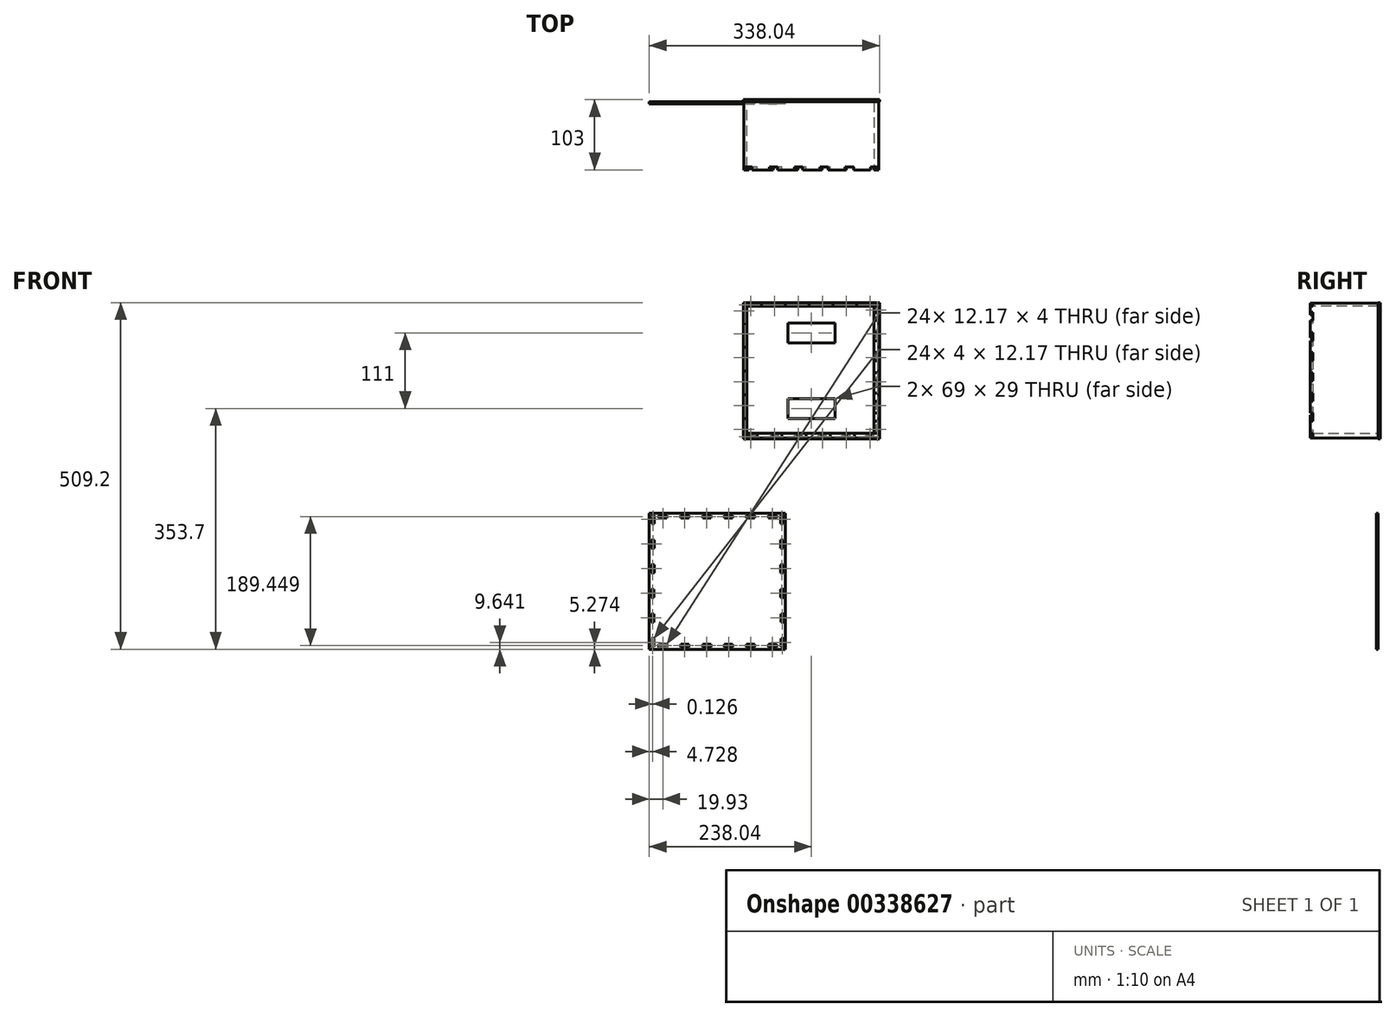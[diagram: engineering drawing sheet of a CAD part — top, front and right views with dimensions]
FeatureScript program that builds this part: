
annotation { "Feature Type Name" : "Feature", "Feature Type Description" : "" }
export const myFeature = defineFeature(function(context is Context, id is Id, definition is map)
    precondition{}
    {
        {
            var Q0;
            Q0=qCreatedBy(makeId("Front.planeOp"),FACE);
            var sketch = newSketch(context, id + "F0", { "sketchPlane" : qUnion([Q0])});
            skLineSegment(sketch, "E0.bottom", {"start": v(-100, 100) * mm, "end": v(100, 100) * mm});
            skLineSegment(sketch, "E0.top", {"start": v(-100, -100) * mm, "end": v(100, -100) * mm});
            skLineSegment(sketch, "E0.left", {"start": v(-100, 100) * mm, "end": v(-100, -100) * mm});
            skLineSegment(sketch, "E0.right", {"start": v(100, 100) * mm, "end": v(100, -100) * mm});
            skPoint(sketch, "E0.middle", {"position": v(0, 0) * mm});
            skLineSegment(sketch, "E1.0", {"start": v(-95, 95) * mm, "end": v(95, 95) * mm, "construction": true});
            skLineSegment(sketch, "E1.1", {"start": v(-95, 95) * mm, "end": v(-95, -95) * mm, "construction": true});
            skLineSegment(sketch, "E1.2", {"start": v(-95, -95) * mm, "end": v(95, -95) * mm, "construction": true});
            skLineSegment(sketch, "E1.3", {"start": v(95, 95) * mm, "end": v(95, -95) * mm, "construction": true});
            skSolve(sketch);
        }
        {
            var Q0;
            Q0 = qSketchRegion(id + "F0", true);
            extrude(context, id + "F1", {"entities" : qUnion([Q0]), "depth" : 3 * mm, "offsetDistance" : 25 * mm});
        }
        {
            var Q0;
            Q0=makeQuery(id+"F1.opExtrude","CAP_FACE",FACE,{"disambiguationData":[OSD([sQuery(id+"F0.wireOp",EDGE,"E0.bottom"),sQuery(id+"F0.wireOp",EDGE,"E0.top"),sQuery(id+"F0.wireOp",EDGE,"E0.left"),sQuery(id+"F0.wireOp",EDGE,"E0.right")])],"isStart":false});
            var sketch = newSketch(context, id + "F2", { "sketchPlane" : qUnion([Q0])});
            skLineSegment(sketch, "E2.0", {"start": v(-95, 95) * mm, "end": v(95, 95) * mm, "construction": true});
            skLineSegment(sketch, "E3.0", {"start": v(-95, 95) * mm, "end": v(-95, -95) * mm, "construction": true});
            skLineSegment(sketch, "E4.0", {"start": v(95, 95) * mm, "end": v(95, -95) * mm, "construction": true});
            skLineSegment(sketch, "E5.0", {"start": v(-95, -95) * mm, "end": v(95, -95) * mm, "construction": true});
            skLineSegment(sketch, "E6.bottom", {"start": v(-95, 99) * mm, "end": v(-82.83, 99) * mm});
            skLineSegment(sketch, "E6.top", {"start": v(-95, 95) * mm, "end": v(-82.83, 95) * mm});
            skLineSegment(sketch, "E6.left", {"start": v(-95, 99) * mm, "end": v(-95, 95) * mm});
            skLineSegment(sketch, "E6.right", {"start": v(-82.83, 99) * mm, "end": v(-82.83, 95) * mm});
            skLineSegment(sketch, "E7.1.0.0", {"start": v(-60, 99) * mm, "end": v(-47.83, 99) * mm});
            skLineSegment(sketch, "E7.1.0.1", {"start": v(-60, 99) * mm, "end": v(-60, 95) * mm});
            skLineSegment(sketch, "E7.1.0.2", {"start": v(-47.83, 99) * mm, "end": v(-47.83, 95) * mm});
            skLineSegment(sketch, "E7.1.0.3", {"start": v(-60, 95) * mm, "end": v(-47.83, 95) * mm});
            skLineSegment(sketch, "E7.2.0.0", {"start": v(-25, 99) * mm, "end": v(-12.83, 99) * mm});
            skLineSegment(sketch, "E7.2.0.1", {"start": v(-25, 99) * mm, "end": v(-25, 95) * mm});
            skLineSegment(sketch, "E7.2.0.2", {"start": v(-12.83, 99) * mm, "end": v(-12.83, 95) * mm});
            skLineSegment(sketch, "E7.2.0.3", {"start": v(-25, 95) * mm, "end": v(-12.83, 95) * mm});
            skLineSegment(sketch, "E7.3.0.0", {"start": v(10, 99) * mm, "end": v(22.17, 99) * mm});
            skLineSegment(sketch, "E7.3.0.1", {"start": v(10, 99) * mm, "end": v(10, 95) * mm});
            skLineSegment(sketch, "E7.3.0.2", {"start": v(22.17, 99) * mm, "end": v(22.17, 95) * mm});
            skLineSegment(sketch, "E7.3.0.3", {"start": v(10, 95) * mm, "end": v(22.17, 95) * mm});
            skLineSegment(sketch, "E7.4.0.0", {"start": v(45, 99) * mm, "end": v(57.17, 99) * mm});
            skLineSegment(sketch, "E7.4.0.1", {"start": v(45, 99) * mm, "end": v(45, 95) * mm});
            skLineSegment(sketch, "E7.4.0.2", {"start": v(57.17, 99) * mm, "end": v(57.17, 95) * mm});
            skLineSegment(sketch, "E7.4.0.3", {"start": v(45, 95) * mm, "end": v(57.17, 95) * mm});
            skLineSegment(sketch, "E7.5.0.0", {"start": v(80, 99) * mm, "end": v(92.17, 99) * mm});
            skLineSegment(sketch, "E7.5.0.1", {"start": v(80, 99) * mm, "end": v(80, 95) * mm});
            skLineSegment(sketch, "E7.5.0.2", {"start": v(92.17, 99) * mm, "end": v(92.17, 95) * mm});
            skLineSegment(sketch, "E7.5.0.3", {"start": v(80, 95) * mm, "end": v(92.17, 95) * mm});
            skLineSegment(sketch, "E7.direction1", {"start": v(-95, 99) * mm, "end": v(-60, 99) * mm, "construction": true});
            skLineSegment(sketch, "E8", {"start": v(-95, 0) * mm, "end": v(95, 0) * mm});
            skLineSegment(sketch, "E9.MirrorCS", {"start": v(-95, -99) * mm, "end": v(-95, -95) * mm});
            skLineSegment(sketch, "E10.MirrorCS", {"start": v(-82.83, -99) * mm, "end": v(-82.83, -95) * mm});
            skLineSegment(sketch, "E11.MirrorCS", {"start": v(-95, -95) * mm, "end": v(-82.83, -95) * mm});
            skLineSegment(sketch, "E12.MirrorCS", {"start": v(-95, -99) * mm, "end": v(-82.83, -99) * mm});
            skLineSegment(sketch, "E13.MirrorCS", {"start": v(-60, -99) * mm, "end": v(-47.83, -99) * mm});
            skLineSegment(sketch, "E14.MirrorCS", {"start": v(-47.83, -99) * mm, "end": v(-47.83, -95) * mm});
            skLineSegment(sketch, "E15.MirrorCS", {"start": v(-60, -99) * mm, "end": v(-60, -95) * mm});
            skLineSegment(sketch, "E16.MirrorCS", {"start": v(-60, -95) * mm, "end": v(-47.83, -95) * mm});
            skLineSegment(sketch, "E17.MirrorCS", {"start": v(-25, -99) * mm, "end": v(-12.83, -99) * mm});
            skLineSegment(sketch, "E18.MirrorCS", {"start": v(-25, -99) * mm, "end": v(-25, -95) * mm});
            skLineSegment(sketch, "E19.MirrorCS", {"start": v(-12.83, -99) * mm, "end": v(-12.83, -95) * mm});
            skLineSegment(sketch, "E20.MirrorCS", {"start": v(-25, -95) * mm, "end": v(-12.83, -95) * mm});
            skLineSegment(sketch, "E21.MirrorCS", {"start": v(10, -99) * mm, "end": v(22.17, -99) * mm});
            skLineSegment(sketch, "E22.MirrorCS", {"start": v(22.17, -99) * mm, "end": v(22.17, -95) * mm});
            skLineSegment(sketch, "E23.MirrorCS", {"start": v(10, -99) * mm, "end": v(10, -95) * mm});
            skLineSegment(sketch, "E24.MirrorCS", {"start": v(10, -95) * mm, "end": v(22.17, -95) * mm});
            skLineSegment(sketch, "E25.MirrorCS", {"start": v(45, -99) * mm, "end": v(57.17, -99) * mm});
            skLineSegment(sketch, "E26.MirrorCS", {"start": v(45, -99) * mm, "end": v(45, -95) * mm});
            skLineSegment(sketch, "E27.MirrorCS", {"start": v(57.17, -99) * mm, "end": v(57.17, -95) * mm});
            skLineSegment(sketch, "E28.MirrorCS", {"start": v(45, -95) * mm, "end": v(57.17, -95) * mm});
            skLineSegment(sketch, "E29.MirrorCS", {"start": v(80, -99) * mm, "end": v(92.17, -99) * mm});
            skLineSegment(sketch, "E30.MirrorCS", {"start": v(80, -99) * mm, "end": v(80, -95) * mm});
            skLineSegment(sketch, "E31.MirrorCS", {"start": v(92.17, -99) * mm, "end": v(92.17, -95) * mm});
            skLineSegment(sketch, "E32.MirrorCS", {"start": v(80, -95) * mm, "end": v(92.17, -95) * mm});
            skLineSegment(sketch, "E33.bottom", {"start": v(99, 95) * mm, "end": v(95, 95) * mm});
            skLineSegment(sketch, "E33.top", {"start": v(99, 82.83) * mm, "end": v(95, 82.83) * mm});
            skLineSegment(sketch, "E33.left", {"start": v(99, 95) * mm, "end": v(99, 82.83) * mm});
            skLineSegment(sketch, "E33.right", {"start": v(95, 95) * mm, "end": v(95, 82.83) * mm});
            skLineSegment(sketch, "E34.1.0.0", {"start": v(99, 47.83) * mm, "end": v(95, 47.83) * mm});
            skLineSegment(sketch, "E34.1.0.1", {"start": v(99, 60) * mm, "end": v(99, 47.83) * mm});
            skLineSegment(sketch, "E34.1.0.2", {"start": v(99, 60) * mm, "end": v(95, 60) * mm});
            skLineSegment(sketch, "E34.1.0.3", {"start": v(95, 60) * mm, "end": v(95, 47.83) * mm});
            skLineSegment(sketch, "E34.2.0.0", {"start": v(99, 12.83) * mm, "end": v(95, 12.83) * mm});
            skLineSegment(sketch, "E34.2.0.1", {"start": v(99, 25) * mm, "end": v(99, 12.83) * mm});
            skLineSegment(sketch, "E34.2.0.2", {"start": v(99, 25) * mm, "end": v(95, 25) * mm});
            skLineSegment(sketch, "E34.2.0.3", {"start": v(95, 25) * mm, "end": v(95, 12.83) * mm});
            skLineSegment(sketch, "E34.3.0.0", {"start": v(99, -22.17) * mm, "end": v(95, -22.17) * mm});
            skLineSegment(sketch, "E34.3.0.1", {"start": v(99, -10) * mm, "end": v(99, -22.17) * mm});
            skLineSegment(sketch, "E34.3.0.2", {"start": v(99, -10) * mm, "end": v(95, -10) * mm});
            skLineSegment(sketch, "E34.3.0.3", {"start": v(95, -10) * mm, "end": v(95, -22.17) * mm});
            skLineSegment(sketch, "E34.4.0.0", {"start": v(99, -57.17) * mm, "end": v(95, -57.17) * mm});
            skLineSegment(sketch, "E34.4.0.1", {"start": v(99, -45) * mm, "end": v(99, -57.17) * mm});
            skLineSegment(sketch, "E34.4.0.2", {"start": v(99, -45) * mm, "end": v(95, -45) * mm});
            skLineSegment(sketch, "E34.4.0.3", {"start": v(95, -45) * mm, "end": v(95, -57.17) * mm});
            skLineSegment(sketch, "E34.5.0.0", {"start": v(99, -92.17) * mm, "end": v(95, -92.17) * mm});
            skLineSegment(sketch, "E34.5.0.1", {"start": v(99, -80) * mm, "end": v(99, -92.17) * mm});
            skLineSegment(sketch, "E34.5.0.2", {"start": v(99, -80) * mm, "end": v(95, -80) * mm});
            skLineSegment(sketch, "E34.5.0.3", {"start": v(95, -80) * mm, "end": v(95, -92.17) * mm});
            skLineSegment(sketch, "E34.direction1", {"start": v(95, 82.83) * mm, "end": v(95, 47.83) * mm, "construction": true});
            skLineSegment(sketch, "E35", {"start": v(0, 100) * mm, "end": v(0, -95) * mm});
            skLineSegment(sketch, "E36.MirrorCS", {"start": v(-99, 60) * mm, "end": v(-95, 60) * mm});
            skLineSegment(sketch, "E37.MirrorCS", {"start": v(-99, 60) * mm, "end": v(-99, 47.83) * mm});
            skLineSegment(sketch, "E38.MirrorCS", {"start": v(-99, 47.83) * mm, "end": v(-95, 47.83) * mm});
            skLineSegment(sketch, "E39.MirrorCS", {"start": v(-95, 60) * mm, "end": v(-95, 47.83) * mm});
            skLineSegment(sketch, "E40.MirrorCS", {"start": v(-99, 25) * mm, "end": v(-95, 25) * mm});
            skLineSegment(sketch, "E41.MirrorCS", {"start": v(-99, 25) * mm, "end": v(-99, 12.83) * mm});
            skLineSegment(sketch, "E42.MirrorCS", {"start": v(-99, 12.83) * mm, "end": v(-95, 12.83) * mm});
            skLineSegment(sketch, "E43.MirrorCS", {"start": v(-95, 25) * mm, "end": v(-95, 12.83) * mm});
            skLineSegment(sketch, "E44.MirrorCS", {"start": v(-99, -10) * mm, "end": v(-95, -10) * mm});
            skLineSegment(sketch, "E45.MirrorCS", {"start": v(-99, -10) * mm, "end": v(-99, -22.17) * mm});
            skLineSegment(sketch, "E46.MirrorCS", {"start": v(-99, -22.17) * mm, "end": v(-95, -22.17) * mm});
            skLineSegment(sketch, "E47.MirrorCS", {"start": v(-95, -10) * mm, "end": v(-95, -22.17) * mm});
            skLineSegment(sketch, "E48.MirrorCS", {"start": v(-99, -45) * mm, "end": v(-95, -45) * mm});
            skLineSegment(sketch, "E49.MirrorCS", {"start": v(-99, -45) * mm, "end": v(-99, -57.17) * mm});
            skLineSegment(sketch, "E50.MirrorCS", {"start": v(-99, -57.17) * mm, "end": v(-95, -57.17) * mm});
            skLineSegment(sketch, "E51.MirrorCS", {"start": v(-95, -45) * mm, "end": v(-95, -57.17) * mm});
            skLineSegment(sketch, "E52.MirrorCS", {"start": v(-99, -80) * mm, "end": v(-95, -80) * mm});
            skLineSegment(sketch, "E53.MirrorCS", {"start": v(-99, -80) * mm, "end": v(-99, -92.17) * mm});
            skLineSegment(sketch, "E54.MirrorCS", {"start": v(-99, -92.17) * mm, "end": v(-95, -92.17) * mm});
            skLineSegment(sketch, "E55.MirrorCS", {"start": v(-95, -80) * mm, "end": v(-95, -92.17) * mm});
            skLineSegment(sketch, "E56.bottom", {"start": v(-95, 81.83) * mm, "end": v(-99, 81.83) * mm});
            skLineSegment(sketch, "E56.top", {"start": v(-95, 94) * mm, "end": v(-99, 94) * mm});
            skLineSegment(sketch, "E56.left", {"start": v(-95, 81.83) * mm, "end": v(-95, 94) * mm});
            skLineSegment(sketch, "E56.right", {"start": v(-99, 81.83) * mm, "end": v(-99, 94) * mm});
            skSolve(sketch);
        }
        {
            var Q0;
            Q0 = qSketchRegion(id + "F2", true);
            var Q1;
            Q1=makeQuery(id+"F1.opExtrude","CAP_FACE",FACE,{"disambiguationData":[OSD([sQuery(id+"F0.wireOp",EDGE,"E0.bottom"),sQuery(id+"F0.wireOp",EDGE,"E0.top"),sQuery(id+"F0.wireOp",EDGE,"E0.left"),sQuery(id+"F0.wireOp",EDGE,"E0.right")])],"isStart":true});
            extrude(context, id + "F3", {"entities" : qUnion([Q0]), "operationType" : NewBodyOperationType.REMOVE, "endBound" : BoundingType.UP_TO_SURFACE, "oppositeDirection" : true, "depth" : 25 * mm, "endBoundEntityFace" : qUnion([Q1]), "offsetDistance" : 25 * mm});
        }
        {
            var Q0;
            Q0=makeQuery(id+"F1.opExtrude","CAP_FACE",FACE,{"disambiguationData":[OSD([sQuery(id+"F0.wireOp",EDGE,"E0.bottom"),sQuery(id+"F0.wireOp",EDGE,"E0.top"),sQuery(id+"F0.wireOp",EDGE,"E0.left"),sQuery(id+"F0.wireOp",EDGE,"E0.right")])],"isStart":false});
            var sketch = newSketch(context, id + "F4", { "sketchPlane" : qUnion([Q0])});
            skLineSegment(sketch, "E57.0", {"start": v(-95, 99) * mm, "end": v(-95, 95) * mm});
            skLineSegment(sketch, "E58.0", {"start": v(-95, 99) * mm, "end": v(-82.83, 99) * mm});
            skLineSegment(sketch, "E59.0", {"start": v(-82.83, 95) * mm, "end": v(-95, 95) * mm});
            skLineSegment(sketch, "E60.0", {"start": v(-82.83, 99) * mm, "end": v(-82.83, 95) * mm});
            skLineSegment(sketch, "E61.0", {"start": v(-60, 99) * mm, "end": v(-47.83, 99) * mm});
            skLineSegment(sketch, "E62.0", {"start": v(-60, 99) * mm, "end": v(-60, 95) * mm});
            skLineSegment(sketch, "E63.0", {"start": v(-47.83, 99) * mm, "end": v(-47.83, 95) * mm});
            skLineSegment(sketch, "E64.0", {"start": v(-47.83, 95) * mm, "end": v(-60, 95) * mm});
            skLineSegment(sketch, "E65.0", {"start": v(-25, 99) * mm, "end": v(-12.83, 99) * mm});
            skLineSegment(sketch, "E66.0", {"start": v(-25, 99) * mm, "end": v(-25, 95) * mm});
            skLineSegment(sketch, "E67.0", {"start": v(-12.83, 99) * mm, "end": v(-12.83, 95) * mm});
            skLineSegment(sketch, "E68.0", {"start": v(-12.83, 95) * mm, "end": v(-25, 95) * mm});
            skLineSegment(sketch, "E69.0", {"start": v(10, 99) * mm, "end": v(22.17, 99) * mm});
            skLineSegment(sketch, "E70.0", {"start": v(22.17, 99) * mm, "end": v(22.17, 95) * mm});
            skLineSegment(sketch, "E71.0", {"start": v(10, 99) * mm, "end": v(10, 95) * mm});
            skLineSegment(sketch, "E72.0", {"start": v(22.17, 95) * mm, "end": v(10, 95) * mm});
            skLineSegment(sketch, "E73.0", {"start": v(45, 99) * mm, "end": v(57.17, 99) * mm});
            skLineSegment(sketch, "E74.0", {"start": v(45, 99) * mm, "end": v(45, 95) * mm});
            skLineSegment(sketch, "E75.0", {"start": v(57.17, 99) * mm, "end": v(57.17, 95) * mm});
            skLineSegment(sketch, "E76.0", {"start": v(57.17, 95) * mm, "end": v(45, 95) * mm});
            skLineSegment(sketch, "E77.0", {"start": v(80, 99) * mm, "end": v(92.17, 99) * mm});
            skLineSegment(sketch, "E78.0", {"start": v(92.17, 99) * mm, "end": v(92.17, 95) * mm});
            skLineSegment(sketch, "E79.0", {"start": v(80, 99) * mm, "end": v(80, 95) * mm});
            skLineSegment(sketch, "E80.0", {"start": v(92.17, 95) * mm, "end": v(80, 95) * mm});
            skSolve(sketch);
        }
        {
            var Q0;
            Q0 = qSketchRegion(id + "F4", true);
            var Q1;
            Q1=makeQuery(id+"F1.opExtrude","CAP_FACE",FACE,{"disambiguationData":[OSD([sQuery(id+"F0.wireOp",EDGE,"E0.bottom"),sQuery(id+"F0.wireOp",EDGE,"E0.top"),sQuery(id+"F0.wireOp",EDGE,"E0.left"),sQuery(id+"F0.wireOp",EDGE,"E0.right")])],"isStart":true});
            extrude(context, id + "F5", {"entities" : qUnion([Q0]), "endBound" : BoundingType.UP_TO_SURFACE, "oppositeDirection" : true, "depth" : 25 * mm, "endBoundEntityFace" : qUnion([Q1]), "offsetDistance" : 25 * mm});
        }
        {
            var Q0;
            Q0=makeQuery(id+"F1.opExtrude","CAP_FACE",FACE,{"disambiguationData":[OSD([sQuery(id+"F0.wireOp",EDGE,"E0.bottom"),sQuery(id+"F0.wireOp",EDGE,"E0.top"),sQuery(id+"F0.wireOp",EDGE,"E0.left"),sQuery(id+"F0.wireOp",EDGE,"E0.right")])],"isStart":false});
            var sketch = newSketch(context, id + "F6", { "sketchPlane" : qUnion([Q0])});
            skLineSegment(sketch, "E81.bottom", {"start": v(-99, 99) * mm, "end": v(99, 99) * mm});
            skLineSegment(sketch, "E81.top", {"start": v(-99, 95) * mm, "end": v(99, 95) * mm});
            skLineSegment(sketch, "E81.left", {"start": v(-99, 99) * mm, "end": v(-99, 95) * mm});
            skLineSegment(sketch, "E81.right", {"start": v(99, 99) * mm, "end": v(99, 95) * mm});
            skSolve(sketch);
        }
        {
            var Q0;
            Q0 = qSketchRegion(id + "F6", true);
            extrude(context, id + "F7", {"entities" : qUnion([Q0]), "depth" : 100 * mm, "offsetDistance" : 25 * mm});
        }
        {
            var Q0;
            Q0=makeQuery(id+"F5.opExtrude","SWEPT_BODY",BODY,{"disambiguationData":[OSD([sQuery(id+"F4.wireOp",EDGE,"E57.0"),sQuery(id+"F4.wireOp",EDGE,"E58.0"),sQuery(id+"F4.wireOp",EDGE,"E59.0"),sQuery(id+"F4.wireOp",EDGE,"E60.0")])]});
            var Q1;
            Q1=makeQuery(id+"F5.opExtrude","SWEPT_BODY",BODY,{"disambiguationData":[OSD([sQuery(id+"F4.wireOp",EDGE,"E61.0"),sQuery(id+"F4.wireOp",EDGE,"E62.0"),sQuery(id+"F4.wireOp",EDGE,"E63.0"),sQuery(id+"F4.wireOp",EDGE,"E64.0")])]});
            var Q2;
            Q2=makeQuery(id+"F5.opExtrude","SWEPT_BODY",BODY,{"disambiguationData":[OSD([sQuery(id+"F4.wireOp",EDGE,"E65.0"),sQuery(id+"F4.wireOp",EDGE,"E66.0"),sQuery(id+"F4.wireOp",EDGE,"E67.0"),sQuery(id+"F4.wireOp",EDGE,"E68.0")])]});
            var Q3;
            Q3=makeQuery(id+"F5.opExtrude","SWEPT_BODY",BODY,{"disambiguationData":[OSD([sQuery(id+"F4.wireOp",EDGE,"E69.0"),sQuery(id+"F4.wireOp",EDGE,"E70.0"),sQuery(id+"F4.wireOp",EDGE,"E71.0"),sQuery(id+"F4.wireOp",EDGE,"E72.0")])]});
            var Q4;
            Q4=makeQuery(id+"F5.opExtrude","SWEPT_BODY",BODY,{"disambiguationData":[OSD([sQuery(id+"F4.wireOp",EDGE,"E73.0"),sQuery(id+"F4.wireOp",EDGE,"E74.0"),sQuery(id+"F4.wireOp",EDGE,"E75.0"),sQuery(id+"F4.wireOp",EDGE,"E76.0")])]});
            var Q5;
            Q5=makeQuery(id+"F5.opExtrude","SWEPT_BODY",BODY,{"disambiguationData":[OSD([sQuery(id+"F4.wireOp",EDGE,"E77.0"),sQuery(id+"F4.wireOp",EDGE,"E78.0"),sQuery(id+"F4.wireOp",EDGE,"E79.0"),sQuery(id+"F4.wireOp",EDGE,"E80.0")])]});
            var Q6;
            Q6=makeQuery(id+"F7.opExtrude","SWEPT_BODY",BODY,{"disambiguationData":[OSD([sQuery(id+"F6.wireOp",EDGE,"E81.bottom"),sQuery(id+"F6.wireOp",EDGE,"E81.top"),sQuery(id+"F6.wireOp",EDGE,"E81.left"),sQuery(id+"F6.wireOp",EDGE,"E81.right")])]});
            booleanBodies(context, id + "F8", {"operationType" : BooleanOperationType.UNION, "tools" : qUnion([Q0, Q1, Q2, Q3, Q4, Q5, Q6])});
        }
        {
            var Q0;
            Q0=makeQuery(id+"F1.opExtrude","CAP_FACE",FACE,{"disambiguationData":[OSD([sQuery(id+"F0.wireOp",EDGE,"E0.bottom"),sQuery(id+"F0.wireOp",EDGE,"E0.top"),sQuery(id+"F0.wireOp",EDGE,"E0.left"),sQuery(id+"F0.wireOp",EDGE,"E0.right")])],"isStart":false});
            var sketch = newSketch(context, id + "F9", { "sketchPlane" : qUnion([Q0])});
            skLineSegment(sketch, "E82.0", {"start": v(99, 95) * mm, "end": v(99, 82.83) * mm});
            skLineSegment(sketch, "E83.0", {"start": v(99, 82.83) * mm, "end": v(95, 82.83) * mm});
            skLineSegment(sketch, "E84.0", {"start": v(95, 95) * mm, "end": v(99, 95) * mm});
            skLineSegment(sketch, "E85.0", {"start": v(95, 82.83) * mm, "end": v(95, 95) * mm});
            skLineSegment(sketch, "E86.0", {"start": v(99, 60) * mm, "end": v(99, 47.83) * mm});
            skLineSegment(sketch, "E87.0", {"start": v(99, 60) * mm, "end": v(95, 60) * mm});
            skLineSegment(sketch, "E88.0", {"start": v(99, 47.83) * mm, "end": v(95, 47.83) * mm});
            skLineSegment(sketch, "E89.0", {"start": v(95, 47.83) * mm, "end": v(95, 60) * mm});
            skLineSegment(sketch, "E90.0", {"start": v(99, 25) * mm, "end": v(99, 12.83) * mm});
            skLineSegment(sketch, "E91.0", {"start": v(99, 25) * mm, "end": v(95, 25) * mm});
            skLineSegment(sketch, "E92.0", {"start": v(95, 12.83) * mm, "end": v(95, 25) * mm});
            skLineSegment(sketch, "E93.0", {"start": v(99, 12.83) * mm, "end": v(95, 12.83) * mm});
            skLineSegment(sketch, "E94.0", {"start": v(99, -10) * mm, "end": v(99, -22.17) * mm});
            skLineSegment(sketch, "E95.0", {"start": v(99, -10) * mm, "end": v(95, -10) * mm});
            skLineSegment(sketch, "E96.0", {"start": v(95, -22.17) * mm, "end": v(95, -10) * mm});
            skLineSegment(sketch, "E97.0", {"start": v(99, -22.17) * mm, "end": v(95, -22.17) * mm});
            skLineSegment(sketch, "E98.0", {"start": v(99, -45) * mm, "end": v(99, -57.17) * mm});
            skLineSegment(sketch, "E99.0", {"start": v(99, -45) * mm, "end": v(95, -45) * mm});
            skLineSegment(sketch, "E100.0", {"start": v(99, -57.17) * mm, "end": v(95, -57.17) * mm});
            skLineSegment(sketch, "E101.0", {"start": v(95, -57.17) * mm, "end": v(95, -45) * mm});
            skLineSegment(sketch, "E102.0", {"start": v(99, -80) * mm, "end": v(99, -92.17) * mm});
            skLineSegment(sketch, "E103.0", {"start": v(99, -80) * mm, "end": v(95, -80) * mm});
            skLineSegment(sketch, "E104.0", {"start": v(95, -92.17) * mm, "end": v(95, -80) * mm});
            skLineSegment(sketch, "E105.0", {"start": v(99, -92.17) * mm, "end": v(95, -92.17) * mm});
            skSolve(sketch);
        }
        {
            var Q0;
            Q0 = qSketchRegion(id + "F9", true);
            var Q1;
            Q1=makeQuery(id+"F1.opExtrude","CAP_FACE",FACE,{"disambiguationData":[OSD([sQuery(id+"F0.wireOp",EDGE,"E0.bottom"),sQuery(id+"F0.wireOp",EDGE,"E0.top"),sQuery(id+"F0.wireOp",EDGE,"E0.left"),sQuery(id+"F0.wireOp",EDGE,"E0.right")])],"isStart":true});
            extrude(context, id + "F10", {"entities" : qUnion([Q0]), "endBound" : BoundingType.UP_TO_SURFACE, "oppositeDirection" : true, "depth" : 25 * mm, "endBoundEntityFace" : qUnion([Q1]), "offsetDistance" : 25 * mm});
        }
        {
            var Q0;
            Q0=makeQuery(id+"F1.opExtrude","CAP_FACE",FACE,{"disambiguationData":[OSD([sQuery(id+"F0.wireOp",EDGE,"E0.bottom"),sQuery(id+"F0.wireOp",EDGE,"E0.top"),sQuery(id+"F0.wireOp",EDGE,"E0.left"),sQuery(id+"F0.wireOp",EDGE,"E0.right")])],"isStart":false});
            var sketch = newSketch(context, id + "F11", { "sketchPlane" : qUnion([Q0])});
            skLineSegment(sketch, "E106.bottom", {"start": v(99, 99) * mm, "end": v(92.17, 99) * mm});
            skLineSegment(sketch, "E106.top", {"start": v(99, -99) * mm, "end": v(92.17, -99) * mm});
            skLineSegment(sketch, "E106.left", {"start": v(99, 99) * mm, "end": v(99, -99) * mm});
            skLineSegment(sketch, "E106.right", {"start": v(92.17, 99) * mm, "end": v(92.17, -99) * mm});
            skSolve(sketch);
        }
        {
            var Q0;
            Q0 = qSketchRegion(id + "F11", true);
            extrude(context, id + "F12", {"entities" : qUnion([Q0]), "depth" : 100 * mm, "offsetDistance" : 25 * mm});
        }
        {
            var Q0;
            Q0=makeQuery(id+"F5.opExtrude","SWEPT_BODY",BODY,{"disambiguationData":[OSD([sQuery(id+"F4.wireOp",EDGE,"E57.0"),sQuery(id+"F4.wireOp",EDGE,"E58.0"),sQuery(id+"F4.wireOp",EDGE,"E59.0"),sQuery(id+"F4.wireOp",EDGE,"E60.0")])]});
            var Q1;
            Q1=makeQuery(id+"F10.opExtrude","SWEPT_BODY",BODY,{"disambiguationData":[OSD([sQuery(id+"F9.wireOp",EDGE,"E82.0"),sQuery(id+"F9.wireOp",EDGE,"E83.0"),sQuery(id+"F9.wireOp",EDGE,"E84.0"),sQuery(id+"F9.wireOp",EDGE,"E85.0")])]});
            var Q2;
            Q2=makeQuery(id+"F10.opExtrude","SWEPT_BODY",BODY,{"disambiguationData":[OSD([sQuery(id+"F9.wireOp",EDGE,"E86.0"),sQuery(id+"F9.wireOp",EDGE,"E87.0"),sQuery(id+"F9.wireOp",EDGE,"E88.0"),sQuery(id+"F9.wireOp",EDGE,"E89.0")])]});
            var Q3;
            Q3=makeQuery(id+"F10.opExtrude","SWEPT_BODY",BODY,{"disambiguationData":[OSD([sQuery(id+"F9.wireOp",EDGE,"E90.0"),sQuery(id+"F9.wireOp",EDGE,"E91.0"),sQuery(id+"F9.wireOp",EDGE,"E92.0"),sQuery(id+"F9.wireOp",EDGE,"E93.0")])]});
            var Q4;
            Q4=makeQuery(id+"F10.opExtrude","SWEPT_BODY",BODY,{"disambiguationData":[OSD([sQuery(id+"F9.wireOp",EDGE,"E94.0"),sQuery(id+"F9.wireOp",EDGE,"E95.0"),sQuery(id+"F9.wireOp",EDGE,"E96.0"),sQuery(id+"F9.wireOp",EDGE,"E97.0")])]});
            var Q5;
            Q5=makeQuery(id+"F10.opExtrude","SWEPT_BODY",BODY,{"disambiguationData":[OSD([sQuery(id+"F9.wireOp",EDGE,"E98.0"),sQuery(id+"F9.wireOp",EDGE,"E99.0"),sQuery(id+"F9.wireOp",EDGE,"E100.0"),sQuery(id+"F9.wireOp",EDGE,"E101.0")])]});
            var Q6;
            Q6=makeQuery(id+"F10.opExtrude","SWEPT_BODY",BODY,{"disambiguationData":[OSD([sQuery(id+"F9.wireOp",EDGE,"E102.0"),sQuery(id+"F9.wireOp",EDGE,"E103.0"),sQuery(id+"F9.wireOp",EDGE,"E104.0"),sQuery(id+"F9.wireOp",EDGE,"E105.0")])]});
            var Q7;
            Q7=makeQuery(id+"F12.opExtrude","SWEPT_BODY",BODY,{"disambiguationData":[OSD([sQuery(id+"F11.wireOp",EDGE,"E106.bottom"),sQuery(id+"F11.wireOp",EDGE,"E106.top"),sQuery(id+"F11.wireOp",EDGE,"E106.left"),sQuery(id+"F11.wireOp",EDGE,"E106.right")])]});
            booleanBodies(context, id + "F13", {"operationType" : BooleanOperationType.UNION, "tools" : qUnion([Q0, Q1, Q2, Q3, Q4, Q5, Q6, Q7])});
        }
        {
            var Q0;
            Q0=makeQuery(id+"F1.opExtrude","CAP_FACE",FACE,{"disambiguationData":[OSD([sQuery(id+"F0.wireOp",EDGE,"E0.bottom"),sQuery(id+"F0.wireOp",EDGE,"E0.top"),sQuery(id+"F0.wireOp",EDGE,"E0.left"),sQuery(id+"F0.wireOp",EDGE,"E0.right")])],"isStart":false});
            var sketch = newSketch(context, id + "F14", { "sketchPlane" : qUnion([Q0])});
            skLineSegment(sketch, "E107.0", {"start": v(80, -99) * mm, "end": v(92.17, -99) * mm});
            skLineSegment(sketch, "E108.0", {"start": v(80, -99) * mm, "end": v(80, -95) * mm});
            skLineSegment(sketch, "E109.0", {"start": v(92.17, -95) * mm, "end": v(92.17, -99) * mm});
            skLineSegment(sketch, "E110.0", {"start": v(92.17, -95) * mm, "end": v(80, -95) * mm});
            skLineSegment(sketch, "E111.0", {"start": v(45, -99) * mm, "end": v(57.17, -99) * mm});
            skLineSegment(sketch, "E112.0", {"start": v(57.17, -99) * mm, "end": v(57.17, -95) * mm});
            skLineSegment(sketch, "E113.0", {"start": v(45, -99) * mm, "end": v(45, -95) * mm});
            skLineSegment(sketch, "E114.0", {"start": v(57.17, -95) * mm, "end": v(45, -95) * mm});
            skLineSegment(sketch, "E115.0", {"start": v(10, -99) * mm, "end": v(22.17, -99) * mm});
            skLineSegment(sketch, "E116.0", {"start": v(22.17, -99) * mm, "end": v(22.17, -95) * mm});
            skLineSegment(sketch, "E117.0", {"start": v(22.17, -95) * mm, "end": v(10, -95) * mm});
            skLineSegment(sketch, "E118.0", {"start": v(10, -99) * mm, "end": v(10, -95) * mm});
            skLineSegment(sketch, "E119.0", {"start": v(-25, -99) * mm, "end": v(-12.83, -99) * mm});
            skLineSegment(sketch, "E120.0", {"start": v(-12.83, -99) * mm, "end": v(-12.83, -95) * mm});
            skLineSegment(sketch, "E121.0", {"start": v(-25, -99) * mm, "end": v(-25, -95) * mm});
            skLineSegment(sketch, "E122.0", {"start": v(-12.83, -95) * mm, "end": v(-25, -95) * mm});
            skLineSegment(sketch, "E123.0", {"start": v(-60, -99) * mm, "end": v(-47.83, -99) * mm});
            skLineSegment(sketch, "E124.0", {"start": v(-47.83, -99) * mm, "end": v(-47.83, -95) * mm});
            skLineSegment(sketch, "E125.0", {"start": v(-60, -99) * mm, "end": v(-60, -95) * mm});
            skLineSegment(sketch, "E126.0", {"start": v(-47.83, -95) * mm, "end": v(-60, -95) * mm});
            skLineSegment(sketch, "E127.0", {"start": v(-95, -99) * mm, "end": v(-82.83, -99) * mm});
            skLineSegment(sketch, "E128.0", {"start": v(-82.83, -95) * mm, "end": v(-95, -95) * mm});
            skLineSegment(sketch, "E129.0", {"start": v(-95, -99) * mm, "end": v(-95, -95) * mm});
            skLineSegment(sketch, "E130.0", {"start": v(-82.83, -99) * mm, "end": v(-82.83, -95) * mm});
            skSolve(sketch);
        }
        {
            var Q0;
            Q0 = qSketchRegion(id + "F14", true);
            var Q1;
            Q1=makeQuery(id+"F1.opExtrude","CAP_FACE",FACE,{"disambiguationData":[OSD([sQuery(id+"F0.wireOp",EDGE,"E0.bottom"),sQuery(id+"F0.wireOp",EDGE,"E0.top"),sQuery(id+"F0.wireOp",EDGE,"E0.left"),sQuery(id+"F0.wireOp",EDGE,"E0.right")])],"isStart":true});
            extrude(context, id + "F15", {"entities" : qUnion([Q0]), "endBound" : BoundingType.UP_TO_SURFACE, "oppositeDirection" : true, "depth" : 25 * mm, "endBoundEntityFace" : qUnion([Q1]), "offsetDistance" : 25 * mm});
        }
        {
            var Q0;
            Q0=makeQuery(id+"F1.opExtrude","CAP_FACE",FACE,{"disambiguationData":[OSD([sQuery(id+"F0.wireOp",EDGE,"E0.bottom"),sQuery(id+"F0.wireOp",EDGE,"E0.top"),sQuery(id+"F0.wireOp",EDGE,"E0.left"),sQuery(id+"F0.wireOp",EDGE,"E0.right")])],"isStart":false});
            var sketch = newSketch(context, id + "F16", { "sketchPlane" : qUnion([Q0])});
            skLineSegment(sketch, "E131.bottom", {"start": v(99, -99) * mm, "end": v(-99, -99) * mm});
            skLineSegment(sketch, "E131.top", {"start": v(99, -92.17) * mm, "end": v(-99, -92.17) * mm});
            skLineSegment(sketch, "E131.left", {"start": v(99, -99) * mm, "end": v(99, -92.17) * mm});
            skLineSegment(sketch, "E131.right", {"start": v(-99, -99) * mm, "end": v(-99, -92.17) * mm});
            skSolve(sketch);
        }
        {
            var Q0;
            Q0 = qSketchRegion(id + "F16", true);
            extrude(context, id + "F17", {"entities" : qUnion([Q0]), "depth" : 100 * mm, "offsetDistance" : 25 * mm});
        }
        {
            var Q0;
            Q0=makeQuery(id+"F5.opExtrude","SWEPT_BODY",BODY,{"disambiguationData":[OSD([sQuery(id+"F4.wireOp",EDGE,"E57.0"),sQuery(id+"F4.wireOp",EDGE,"E58.0"),sQuery(id+"F4.wireOp",EDGE,"E59.0"),sQuery(id+"F4.wireOp",EDGE,"E60.0")])]});
            var Q1;
            Q1=makeQuery(id+"F15.opExtrude","SWEPT_BODY",BODY,{"disambiguationData":[OSD([sQuery(id+"F14.wireOp",EDGE,"E107.0"),sQuery(id+"F14.wireOp",EDGE,"E108.0"),sQuery(id+"F14.wireOp",EDGE,"E109.0"),sQuery(id+"F14.wireOp",EDGE,"E110.0")])]});
            var Q2;
            Q2=makeQuery(id+"F15.opExtrude","SWEPT_BODY",BODY,{"disambiguationData":[OSD([sQuery(id+"F14.wireOp",EDGE,"E111.0"),sQuery(id+"F14.wireOp",EDGE,"E112.0"),sQuery(id+"F14.wireOp",EDGE,"E113.0"),sQuery(id+"F14.wireOp",EDGE,"E114.0")])]});
            var Q3;
            Q3=makeQuery(id+"F15.opExtrude","SWEPT_BODY",BODY,{"disambiguationData":[OSD([sQuery(id+"F14.wireOp",EDGE,"E115.0"),sQuery(id+"F14.wireOp",EDGE,"E116.0"),sQuery(id+"F14.wireOp",EDGE,"E117.0"),sQuery(id+"F14.wireOp",EDGE,"E118.0")])]});
            var Q4;
            Q4=makeQuery(id+"F15.opExtrude","SWEPT_BODY",BODY,{"disambiguationData":[OSD([sQuery(id+"F14.wireOp",EDGE,"E119.0"),sQuery(id+"F14.wireOp",EDGE,"E120.0"),sQuery(id+"F14.wireOp",EDGE,"E121.0"),sQuery(id+"F14.wireOp",EDGE,"E122.0")])]});
            var Q5;
            Q5=makeQuery(id+"F15.opExtrude","SWEPT_BODY",BODY,{"disambiguationData":[OSD([sQuery(id+"F14.wireOp",EDGE,"E123.0"),sQuery(id+"F14.wireOp",EDGE,"E124.0"),sQuery(id+"F14.wireOp",EDGE,"E125.0"),sQuery(id+"F14.wireOp",EDGE,"E126.0")])]});
            var Q6;
            Q6=makeQuery(id+"F15.opExtrude","SWEPT_BODY",BODY,{"disambiguationData":[OSD([sQuery(id+"F14.wireOp",EDGE,"E127.0"),sQuery(id+"F14.wireOp",EDGE,"E128.0"),sQuery(id+"F14.wireOp",EDGE,"E129.0"),sQuery(id+"F14.wireOp",EDGE,"E130.0")])]});
            var Q7;
            Q7=makeQuery(id+"F17.opExtrude","SWEPT_BODY",BODY,{"disambiguationData":[OSD([sQuery(id+"F16.wireOp",EDGE,"E131.bottom"),sQuery(id+"F16.wireOp",EDGE,"E131.top"),sQuery(id+"F16.wireOp",EDGE,"E131.left"),sQuery(id+"F16.wireOp",EDGE,"E131.right")])]});
            booleanBodies(context, id + "F18", {"operationType" : BooleanOperationType.UNION, "tools" : qUnion([Q0, Q1, Q2, Q3, Q4, Q5, Q6, Q7])});
        }
        {
            var Q0;
            Q0=makeQuery(id+"F1.opExtrude","CAP_FACE",FACE,{"disambiguationData":[OSD([sQuery(id+"F0.wireOp",EDGE,"E0.bottom"),sQuery(id+"F0.wireOp",EDGE,"E0.top"),sQuery(id+"F0.wireOp",EDGE,"E0.left"),sQuery(id+"F0.wireOp",EDGE,"E0.right")])],"isStart":false});
            var sketch = newSketch(context, id + "F19", { "sketchPlane" : qUnion([Q0])});
            skLineSegment(sketch, "E132.0", {"start": v(-99, -80) * mm, "end": v(-95, -80) * mm});
            skLineSegment(sketch, "E133.0", {"start": v(-99, -80) * mm, "end": v(-99, -92.17) * mm});
            skLineSegment(sketch, "E134.0", {"start": v(-95, -92.17) * mm, "end": v(-99, -92.17) * mm});
            skLineSegment(sketch, "E135.0", {"start": v(-95, -92.17) * mm, "end": v(-95, -80) * mm});
            skLineSegment(sketch, "E136.0", {"start": v(-99, -45) * mm, "end": v(-99, -57.17) * mm});
            skLineSegment(sketch, "E137.0", {"start": v(-99, -57.17) * mm, "end": v(-95, -57.17) * mm});
            skLineSegment(sketch, "E138.0", {"start": v(-95, -57.17) * mm, "end": v(-95, -45) * mm});
            skLineSegment(sketch, "E139.0", {"start": v(-99, -45) * mm, "end": v(-95, -45) * mm});
            skLineSegment(sketch, "E140.0", {"start": v(-99, -10) * mm, "end": v(-99, -22.17) * mm});
            skLineSegment(sketch, "E141.0", {"start": v(-99, -22.17) * mm, "end": v(-95, -22.17) * mm});
            skLineSegment(sketch, "E142.0", {"start": v(-95, -22.17) * mm, "end": v(-95, -10) * mm});
            skLineSegment(sketch, "E143.0", {"start": v(-99, -10) * mm, "end": v(-95, -10) * mm});
            skLineSegment(sketch, "E144.0", {"start": v(-99, 25) * mm, "end": v(-99, 12.83) * mm});
            skLineSegment(sketch, "E145.0", {"start": v(-99, 12.83) * mm, "end": v(-95, 12.83) * mm});
            skLineSegment(sketch, "E146.0", {"start": v(-95, 12.83) * mm, "end": v(-95, 25) * mm});
            skLineSegment(sketch, "E147.0", {"start": v(-99, 25) * mm, "end": v(-95, 25) * mm});
            skLineSegment(sketch, "E148.0", {"start": v(-99, 60) * mm, "end": v(-99, 47.83) * mm});
            skLineSegment(sketch, "E149.0", {"start": v(-99, 47.83) * mm, "end": v(-95, 47.83) * mm});
            skLineSegment(sketch, "E150.0", {"start": v(-95, 47.83) * mm, "end": v(-95, 60) * mm});
            skLineSegment(sketch, "E151.0", {"start": v(-99, 60) * mm, "end": v(-95, 60) * mm});
            skLineSegment(sketch, "E152.0", {"start": v(-99, 81.83) * mm, "end": v(-99, 94) * mm});
            skLineSegment(sketch, "E153.0", {"start": v(-95, 81.83) * mm, "end": v(-99, 81.83) * mm});
            skLineSegment(sketch, "E154.0", {"start": v(-95, 94) * mm, "end": v(-95, 81.83) * mm});
            skLineSegment(sketch, "E155.0", {"start": v(-95, 94) * mm, "end": v(-99, 94) * mm});
            skSolve(sketch);
        }
        {
            var Q0;
            Q0 = qSketchRegion(id + "F19", true);
            var Q1;
            Q1=makeQuery(id+"F1.opExtrude","CAP_FACE",FACE,{"disambiguationData":[OSD([sQuery(id+"F0.wireOp",EDGE,"E0.bottom"),sQuery(id+"F0.wireOp",EDGE,"E0.top"),sQuery(id+"F0.wireOp",EDGE,"E0.left"),sQuery(id+"F0.wireOp",EDGE,"E0.right")])],"isStart":true});
            extrude(context, id + "F20", {"entities" : qUnion([Q0]), "endBound" : BoundingType.UP_TO_SURFACE, "oppositeDirection" : true, "depth" : 25 * mm, "endBoundEntityFace" : qUnion([Q1]), "offsetDistance" : 25 * mm});
        }
        {
            var Q0;
            Q0=makeQuery(id+"F1.opExtrude","CAP_FACE",FACE,{"disambiguationData":[OSD([sQuery(id+"F0.wireOp",EDGE,"E0.bottom"),sQuery(id+"F0.wireOp",EDGE,"E0.top"),sQuery(id+"F0.wireOp",EDGE,"E0.left"),sQuery(id+"F0.wireOp",EDGE,"E0.right")])],"isStart":false});
            var sketch = newSketch(context, id + "F21", { "sketchPlane" : qUnion([Q0])});
            skLineSegment(sketch, "E156.bottom", {"start": v(-99, -99) * mm, "end": v(-95, -99) * mm});
            skLineSegment(sketch, "E156.top", {"start": v(-99, 99) * mm, "end": v(-95, 99) * mm});
            skLineSegment(sketch, "E156.left", {"start": v(-99, -99) * mm, "end": v(-99, 99) * mm});
            skLineSegment(sketch, "E156.right", {"start": v(-95, -99) * mm, "end": v(-95, 99) * mm});
            skSolve(sketch);
        }
        {
            var Q0;
            Q0 = qSketchRegion(id + "F21", true);
            extrude(context, id + "F22", {"entities" : qUnion([Q0]), "depth" : 100 * mm, "offsetDistance" : 25 * mm});
        }
        {
            var Q0;
            Q0=makeQuery(id+"F5.opExtrude","SWEPT_BODY",BODY,{"disambiguationData":[OSD([sQuery(id+"F4.wireOp",EDGE,"E57.0"),sQuery(id+"F4.wireOp",EDGE,"E58.0"),sQuery(id+"F4.wireOp",EDGE,"E59.0"),sQuery(id+"F4.wireOp",EDGE,"E60.0")])]});
            var Q1;
            Q1=makeQuery(id+"F20.opExtrude","SWEPT_BODY",BODY,{"disambiguationData":[OSD([sQuery(id+"F19.wireOp",EDGE,"E132.0"),sQuery(id+"F19.wireOp",EDGE,"E133.0"),sQuery(id+"F19.wireOp",EDGE,"E134.0"),sQuery(id+"F19.wireOp",EDGE,"E135.0")])]});
            var Q2;
            Q2=makeQuery(id+"F20.opExtrude","SWEPT_BODY",BODY,{"disambiguationData":[OSD([sQuery(id+"F19.wireOp",EDGE,"E136.0"),sQuery(id+"F19.wireOp",EDGE,"E137.0"),sQuery(id+"F19.wireOp",EDGE,"E138.0"),sQuery(id+"F19.wireOp",EDGE,"E139.0")])]});
            var Q3;
            Q3=makeQuery(id+"F20.opExtrude","SWEPT_BODY",BODY,{"disambiguationData":[OSD([sQuery(id+"F19.wireOp",EDGE,"E140.0"),sQuery(id+"F19.wireOp",EDGE,"E141.0"),sQuery(id+"F19.wireOp",EDGE,"E142.0"),sQuery(id+"F19.wireOp",EDGE,"E143.0")])]});
            var Q4;
            Q4=makeQuery(id+"F20.opExtrude","SWEPT_BODY",BODY,{"disambiguationData":[OSD([sQuery(id+"F19.wireOp",EDGE,"E144.0"),sQuery(id+"F19.wireOp",EDGE,"E145.0"),sQuery(id+"F19.wireOp",EDGE,"E146.0"),sQuery(id+"F19.wireOp",EDGE,"E147.0")])]});
            var Q5;
            Q5=makeQuery(id+"F20.opExtrude","SWEPT_BODY",BODY,{"disambiguationData":[OSD([sQuery(id+"F19.wireOp",EDGE,"E148.0"),sQuery(id+"F19.wireOp",EDGE,"E149.0"),sQuery(id+"F19.wireOp",EDGE,"E150.0"),sQuery(id+"F19.wireOp",EDGE,"E151.0")])]});
            var Q6;
            Q6=makeQuery(id+"F20.opExtrude","SWEPT_BODY",BODY,{"disambiguationData":[OSD([sQuery(id+"F19.wireOp",EDGE,"E152.0"),sQuery(id+"F19.wireOp",EDGE,"E153.0"),sQuery(id+"F19.wireOp",EDGE,"E154.0"),sQuery(id+"F19.wireOp",EDGE,"E155.0")])]});
            var Q7;
            Q7=makeQuery(id+"F22.opExtrude","SWEPT_BODY",BODY,{"disambiguationData":[OSD([sQuery(id+"F21.wireOp",EDGE,"E156.bottom"),sQuery(id+"F21.wireOp",EDGE,"E156.top"),sQuery(id+"F21.wireOp",EDGE,"E156.left"),sQuery(id+"F21.wireOp",EDGE,"E156.right")])]});
            booleanBodies(context, id + "F23", {"operationType" : BooleanOperationType.UNION, "tools" : qUnion([Q0, Q1, Q2, Q3, Q4, Q5, Q6, Q7])});
        }
        {
            var Q0;
            Q0=makeQuery(id+"F8.opBoolean","MERGE",FACE,{"derivedFrom":[makeQuery(id+"F5.opExtrude","SWEPT_FACE",FACE,{"disambiguationData":[OSD([sQuery(id+"F4.wireOp",EDGE,"E58.0")])]}),makeQuery(id+"F5.opExtrude","SWEPT_FACE",FACE,{"disambiguationData":[OSD([sQuery(id+"F4.wireOp",EDGE,"E61.0")])]}),makeQuery(id+"F5.opExtrude","SWEPT_FACE",FACE,{"disambiguationData":[OSD([sQuery(id+"F4.wireOp",EDGE,"E65.0")])]}),makeQuery(id+"F5.opExtrude","SWEPT_FACE",FACE,{"disambiguationData":[OSD([sQuery(id+"F4.wireOp",EDGE,"E69.0")])]}),makeQuery(id+"F5.opExtrude","SWEPT_FACE",FACE,{"disambiguationData":[OSD([sQuery(id+"F4.wireOp",EDGE,"E73.0")])]}),makeQuery(id+"F5.opExtrude","SWEPT_FACE",FACE,{"disambiguationData":[OSD([sQuery(id+"F4.wireOp",EDGE,"E77.0")])]}),makeQuery(id+"F7.opExtrude","SWEPT_FACE",FACE,{"disambiguationData":[OSD([sQuery(id+"F6.wireOp",EDGE,"E81.bottom")])]})]});
            var sketch = newSketch(context, id + "F24", { "sketchPlane" : qUnion([Q0])});
            skLineSegment(sketch, "E157.bottom", {"start": v(99, -103) * mm, "end": v(86.83, -103) * mm});
            skLineSegment(sketch, "E157.top", {"start": v(99, -99) * mm, "end": v(86.83, -99) * mm});
            skLineSegment(sketch, "E157.left", {"start": v(99, -103) * mm, "end": v(99, -99) * mm});
            skLineSegment(sketch, "E157.right", {"start": v(86.83, -103) * mm, "end": v(86.83, -99) * mm});
            skLineSegment(sketch, "E158.1.0.0", {"start": v(61.8, -103) * mm, "end": v(49.63, -103) * mm});
            skLineSegment(sketch, "E158.1.0.1", {"start": v(61.8, -99) * mm, "end": v(49.63, -99) * mm});
            skLineSegment(sketch, "E158.1.0.2", {"start": v(61.8, -103) * mm, "end": v(61.8, -99) * mm});
            skLineSegment(sketch, "E158.1.0.3", {"start": v(49.63, -103) * mm, "end": v(49.63, -99) * mm});
            skLineSegment(sketch, "E158.2.0.0", {"start": v(24.6, -103) * mm, "end": v(12.43, -103) * mm});
            skLineSegment(sketch, "E158.2.0.1", {"start": v(24.6, -99) * mm, "end": v(12.43, -99) * mm});
            skLineSegment(sketch, "E158.2.0.2", {"start": v(24.6, -103) * mm, "end": v(24.6, -99) * mm});
            skLineSegment(sketch, "E158.2.0.3", {"start": v(12.43, -103) * mm, "end": v(12.43, -99) * mm});
            skLineSegment(sketch, "E158.3.0.0", {"start": v(-12.6, -103) * mm, "end": v(-24.77, -103) * mm});
            skLineSegment(sketch, "E158.3.0.1", {"start": v(-12.6, -99) * mm, "end": v(-24.77, -99) * mm});
            skLineSegment(sketch, "E158.3.0.2", {"start": v(-12.6, -103) * mm, "end": v(-12.6, -99) * mm});
            skLineSegment(sketch, "E158.3.0.3", {"start": v(-24.77, -103) * mm, "end": v(-24.77, -99) * mm});
            skLineSegment(sketch, "E158.4.0.0", {"start": v(-49.8, -103) * mm, "end": v(-61.97, -103) * mm});
            skLineSegment(sketch, "E158.4.0.1", {"start": v(-49.8, -99) * mm, "end": v(-61.97, -99) * mm});
            skLineSegment(sketch, "E158.4.0.2", {"start": v(-49.8, -103) * mm, "end": v(-49.8, -99) * mm});
            skLineSegment(sketch, "E158.4.0.3", {"start": v(-61.97, -103) * mm, "end": v(-61.97, -99) * mm});
            skLineSegment(sketch, "E158.5.0.0", {"start": v(-87, -103) * mm, "end": v(-99.17, -103) * mm});
            skLineSegment(sketch, "E158.5.0.1", {"start": v(-87, -99) * mm, "end": v(-99.17, -99) * mm});
            skLineSegment(sketch, "E158.5.0.2", {"start": v(-87, -103) * mm, "end": v(-87, -99) * mm});
            skLineSegment(sketch, "E158.5.0.3", {"start": v(-99.17, -103) * mm, "end": v(-99.17, -99) * mm});
            skLineSegment(sketch, "E158.direction1", {"start": v(86.83, -103) * mm, "end": v(49.63, -103) * mm, "construction": true});
            skSolve(sketch);
        }
        {
            var Q0;
            Q0 = qSketchRegion(id + "F24", true);
            var Q1;
            Q1=makeQuery(id+"F8.opBoolean","MERGE",FACE,{"derivedFrom":[makeQuery(id+"F5.opExtrude","SWEPT_FACE",FACE,{"disambiguationData":[OSD([sQuery(id+"F4.wireOp",EDGE,"E59.0")])]}),makeQuery(id+"F5.opExtrude","SWEPT_FACE",FACE,{"disambiguationData":[OSD([sQuery(id+"F4.wireOp",EDGE,"E64.0")])]}),makeQuery(id+"F5.opExtrude","SWEPT_FACE",FACE,{"disambiguationData":[OSD([sQuery(id+"F4.wireOp",EDGE,"E68.0")])]}),makeQuery(id+"F5.opExtrude","SWEPT_FACE",FACE,{"disambiguationData":[OSD([sQuery(id+"F4.wireOp",EDGE,"E72.0")])]}),makeQuery(id+"F5.opExtrude","SWEPT_FACE",FACE,{"disambiguationData":[OSD([sQuery(id+"F4.wireOp",EDGE,"E76.0")])]}),makeQuery(id+"F5.opExtrude","SWEPT_FACE",FACE,{"disambiguationData":[OSD([sQuery(id+"F4.wireOp",EDGE,"E80.0")])]}),makeQuery(id+"F7.opExtrude","SWEPT_FACE",FACE,{"disambiguationData":[OSD([sQuery(id+"F6.wireOp",EDGE,"E81.top")])]})]});
            extrude(context, id + "F25", {"entities" : qUnion([Q0]), "operationType" : NewBodyOperationType.REMOVE, "endBound" : BoundingType.UP_TO_SURFACE, "oppositeDirection" : true, "depth" : 25 * mm, "endBoundEntityFace" : qUnion([Q1]), "offsetDistance" : 25 * mm});
        }
        {
            var Q0;
            Q0=makeQuery(id+"F23.opBoolean","MERGE",FACE,{"derivedFrom":[makeQuery(id+"F7.opExtrude","SWEPT_FACE",FACE,{"disambiguationData":[OSD([sQuery(id+"F6.wireOp",EDGE,"E81.left")])]}),makeQuery(id+"F17.opExtrude","SWEPT_FACE",FACE,{"disambiguationData":[OSD([sQuery(id+"F16.wireOp",EDGE,"E131.right")])]}),makeQuery(id+"F20.opExtrude","SWEPT_FACE",FACE,{"disambiguationData":[OSD([sQuery(id+"F19.wireOp",EDGE,"E133.0")])]}),makeQuery(id+"F20.opExtrude","SWEPT_FACE",FACE,{"disambiguationData":[OSD([sQuery(id+"F19.wireOp",EDGE,"E136.0")])]}),makeQuery(id+"F20.opExtrude","SWEPT_FACE",FACE,{"disambiguationData":[OSD([sQuery(id+"F19.wireOp",EDGE,"E140.0")])]}),makeQuery(id+"F20.opExtrude","SWEPT_FACE",FACE,{"disambiguationData":[OSD([sQuery(id+"F19.wireOp",EDGE,"E144.0")])]}),makeQuery(id+"F20.opExtrude","SWEPT_FACE",FACE,{"disambiguationData":[OSD([sQuery(id+"F19.wireOp",EDGE,"E148.0")])]}),makeQuery(id+"F20.opExtrude","SWEPT_FACE",FACE,{"disambiguationData":[OSD([sQuery(id+"F19.wireOp",EDGE,"E152.0")])]}),makeQuery(id+"F22.opExtrude","SWEPT_FACE",FACE,{"disambiguationData":[OSD([sQuery(id+"F21.wireOp",EDGE,"E156.left")])]})]});
            var sketch = newSketch(context, id + "F26", { "sketchPlane" : qUnion([Q0])});
            skLineSegment(sketch, "E159.bottom", {"start": v(103, 82.02) * mm, "end": v(99, 82.02) * mm});
            skLineSegment(sketch, "E159.top", {"start": v(103, 69.85) * mm, "end": v(99, 69.85) * mm});
            skLineSegment(sketch, "E159.left", {"start": v(103, 82.02) * mm, "end": v(103, 69.85) * mm});
            skLineSegment(sketch, "E159.right", {"start": v(99, 82.02) * mm, "end": v(99, 69.85) * mm});
            skLineSegment(sketch, "E160.1.0.0", {"start": v(103, 36.07) * mm, "end": v(99, 36.07) * mm});
            skLineSegment(sketch, "E160.1.0.1", {"start": v(99, 48.24) * mm, "end": v(99, 36.07) * mm});
            skLineSegment(sketch, "E160.1.0.2", {"start": v(103, 48.24) * mm, "end": v(99, 48.24) * mm});
            skLineSegment(sketch, "E160.1.0.3", {"start": v(103, 48.24) * mm, "end": v(103, 36.07) * mm});
            skLineSegment(sketch, "E160.2.0.0", {"start": v(103, 2.3) * mm, "end": v(99, 2.3) * mm});
            skLineSegment(sketch, "E160.2.0.1", {"start": v(99, 14.46) * mm, "end": v(99, 2.3) * mm});
            skLineSegment(sketch, "E160.2.0.2", {"start": v(103, 14.46) * mm, "end": v(99, 14.46) * mm});
            skLineSegment(sketch, "E160.2.0.3", {"start": v(103, 14.46) * mm, "end": v(103, 2.3) * mm});
            skLineSegment(sketch, "E160.3.0.0", {"start": v(103, -31.49) * mm, "end": v(99, -31.49) * mm});
            skLineSegment(sketch, "E160.3.0.1", {"start": v(99, -19.32) * mm, "end": v(99, -31.49) * mm});
            skLineSegment(sketch, "E160.3.0.2", {"start": v(103, -19.32) * mm, "end": v(99, -19.32) * mm});
            skLineSegment(sketch, "E160.3.0.3", {"start": v(103, -19.32) * mm, "end": v(103, -31.49) * mm});
            skLineSegment(sketch, "E160.4.0.0", {"start": v(103, -65.27) * mm, "end": v(99, -65.27) * mm});
            skLineSegment(sketch, "E160.4.0.1", {"start": v(99, -53.1) * mm, "end": v(99, -65.27) * mm});
            skLineSegment(sketch, "E160.4.0.2", {"start": v(103, -53.1) * mm, "end": v(99, -53.1) * mm});
            skLineSegment(sketch, "E160.4.0.3", {"start": v(103, -53.1) * mm, "end": v(103, -65.27) * mm});
            skLineSegment(sketch, "E160.5.0.0", {"start": v(103, -99.05) * mm, "end": v(99, -99.05) * mm});
            skLineSegment(sketch, "E160.5.0.1", {"start": v(99, -86.88) * mm, "end": v(99, -99.05) * mm});
            skLineSegment(sketch, "E160.5.0.2", {"start": v(103, -86.88) * mm, "end": v(99, -86.88) * mm});
            skLineSegment(sketch, "E160.5.0.3", {"start": v(103, -86.88) * mm, "end": v(103, -99.05) * mm});
            skLineSegment(sketch, "E160.direction1", {"start": v(103, 69.85) * mm, "end": v(103, 36.07) * mm, "construction": true});
            skSolve(sketch);
        }
        {
            var Q0;
            Q0 = qSketchRegion(id + "F26", true);
            var Q1;
            Q1=makeQuery(id+"F23.opBoolean","MERGE",FACE,{"derivedFrom":[makeQuery(id+"F20.opExtrude","SWEPT_FACE",FACE,{"disambiguationData":[OSD([sQuery(id+"F19.wireOp",EDGE,"E135.0")])]}),makeQuery(id+"F20.opExtrude","SWEPT_FACE",FACE,{"disambiguationData":[OSD([sQuery(id+"F19.wireOp",EDGE,"E138.0")])]}),makeQuery(id+"F20.opExtrude","SWEPT_FACE",FACE,{"disambiguationData":[OSD([sQuery(id+"F19.wireOp",EDGE,"E142.0")])]}),makeQuery(id+"F20.opExtrude","SWEPT_FACE",FACE,{"disambiguationData":[OSD([sQuery(id+"F19.wireOp",EDGE,"E146.0")])]}),makeQuery(id+"F20.opExtrude","SWEPT_FACE",FACE,{"disambiguationData":[OSD([sQuery(id+"F19.wireOp",EDGE,"E150.0")])]}),makeQuery(id+"F20.opExtrude","SWEPT_FACE",FACE,{"disambiguationData":[OSD([sQuery(id+"F19.wireOp",EDGE,"E154.0")])]}),makeQuery(id+"F22.opExtrude","SWEPT_FACE",FACE,{"disambiguationData":[OSD([sQuery(id+"F21.wireOp",EDGE,"E156.right")])]})]});
            extrude(context, id + "F27", {"entities" : qUnion([Q0]), "operationType" : NewBodyOperationType.REMOVE, "endBound" : BoundingType.UP_TO_SURFACE, "oppositeDirection" : true, "depth" : 25 * mm, "endBoundEntityFace" : qUnion([Q1]), "offsetDistance" : 25 * mm});
        }
        {
            var Q0;
            Q0=makeQuery(id+"F18.opBoolean","MERGE",FACE,{"derivedFrom":[makeQuery(id+"F12.opExtrude","SWEPT_FACE",FACE,{"disambiguationData":[OSD([sQuery(id+"F11.wireOp",EDGE,"E106.top")])]}),makeQuery(id+"F15.opExtrude","SWEPT_FACE",FACE,{"disambiguationData":[OSD([sQuery(id+"F14.wireOp",EDGE,"E107.0")])]}),makeQuery(id+"F15.opExtrude","SWEPT_FACE",FACE,{"disambiguationData":[OSD([sQuery(id+"F14.wireOp",EDGE,"E111.0")])]}),makeQuery(id+"F15.opExtrude","SWEPT_FACE",FACE,{"disambiguationData":[OSD([sQuery(id+"F14.wireOp",EDGE,"E115.0")])]}),makeQuery(id+"F15.opExtrude","SWEPT_FACE",FACE,{"disambiguationData":[OSD([sQuery(id+"F14.wireOp",EDGE,"E119.0")])]}),makeQuery(id+"F15.opExtrude","SWEPT_FACE",FACE,{"disambiguationData":[OSD([sQuery(id+"F14.wireOp",EDGE,"E123.0")])]}),makeQuery(id+"F15.opExtrude","SWEPT_FACE",FACE,{"disambiguationData":[OSD([sQuery(id+"F14.wireOp",EDGE,"E127.0")])]}),makeQuery(id+"F17.opExtrude","SWEPT_FACE",FACE,{"disambiguationData":[OSD([sQuery(id+"F16.wireOp",EDGE,"E131.bottom")])]})]});
            var sketch = newSketch(context, id + "F28", { "sketchPlane" : qUnion([Q0])});
            skLineSegment(sketch, "E161.bottom", {"start": v(-91.49, 103) * mm, "end": v(-79.32, 103) * mm});
            skLineSegment(sketch, "E161.top", {"start": v(-91.49, 99) * mm, "end": v(-79.32, 99) * mm});
            skLineSegment(sketch, "E161.left", {"start": v(-91.49, 103) * mm, "end": v(-91.49, 99) * mm});
            skLineSegment(sketch, "E161.right", {"start": v(-79.32, 103) * mm, "end": v(-79.32, 99) * mm});
            skLineSegment(sketch, "E162.1.0.0", {"start": v(-55.79, 103) * mm, "end": v(-43.62, 103) * mm});
            skLineSegment(sketch, "E162.1.0.1", {"start": v(-43.62, 103) * mm, "end": v(-43.62, 99) * mm});
            skLineSegment(sketch, "E162.1.0.2", {"start": v(-55.79, 99) * mm, "end": v(-43.62, 99) * mm});
            skLineSegment(sketch, "E162.1.0.3", {"start": v(-55.79, 103) * mm, "end": v(-55.79, 99) * mm});
            skLineSegment(sketch, "E162.2.0.0", {"start": v(-20.09, 103) * mm, "end": v(-7.92, 103) * mm});
            skLineSegment(sketch, "E162.2.0.1", {"start": v(-7.92, 103) * mm, "end": v(-7.92, 99) * mm});
            skLineSegment(sketch, "E162.2.0.2", {"start": v(-20.09, 99) * mm, "end": v(-7.92, 99) * mm});
            skLineSegment(sketch, "E162.2.0.3", {"start": v(-20.09, 103) * mm, "end": v(-20.09, 99) * mm});
            skLineSegment(sketch, "E162.3.0.0", {"start": v(15.61, 103) * mm, "end": v(27.78, 103) * mm});
            skLineSegment(sketch, "E162.3.0.1", {"start": v(27.78, 103) * mm, "end": v(27.78, 99) * mm});
            skLineSegment(sketch, "E162.3.0.2", {"start": v(15.61, 99) * mm, "end": v(27.78, 99) * mm});
            skLineSegment(sketch, "E162.3.0.3", {"start": v(15.61, 103) * mm, "end": v(15.61, 99) * mm});
            skLineSegment(sketch, "E162.4.0.0", {"start": v(51.31, 103) * mm, "end": v(63.48, 103) * mm});
            skLineSegment(sketch, "E162.4.0.1", {"start": v(63.48, 103) * mm, "end": v(63.48, 99) * mm});
            skLineSegment(sketch, "E162.4.0.2", {"start": v(51.31, 99) * mm, "end": v(63.48, 99) * mm});
            skLineSegment(sketch, "E162.4.0.3", {"start": v(51.31, 103) * mm, "end": v(51.31, 99) * mm});
            skLineSegment(sketch, "E162.5.0.0", {"start": v(87.01, 103) * mm, "end": v(99.18, 103) * mm});
            skLineSegment(sketch, "E162.5.0.1", {"start": v(99.18, 103) * mm, "end": v(99.18, 99) * mm});
            skLineSegment(sketch, "E162.5.0.2", {"start": v(87.01, 99) * mm, "end": v(99.18, 99) * mm});
            skLineSegment(sketch, "E162.5.0.3", {"start": v(87.01, 103) * mm, "end": v(87.01, 99) * mm});
            skLineSegment(sketch, "E162.direction1", {"start": v(-91.49, 103) * mm, "end": v(-55.79, 103) * mm, "construction": true});
            skSolve(sketch);
        }
        {
            var Q0;
            Q0 = qSketchRegion(id + "F28", true);
            var Q1;
            Q1=makeQuery(id+"F17.opExtrude","SWEPT_FACE",FACE,{"disambiguationData":[OSD([sQuery(id+"F16.wireOp",EDGE,"E131.top")])]});
            extrude(context, id + "F29", {"entities" : qUnion([Q0]), "operationType" : NewBodyOperationType.REMOVE, "endBound" : BoundingType.UP_TO_SURFACE, "oppositeDirection" : true, "depth" : 25 * mm, "endBoundEntityFace" : qUnion([Q1]), "offsetDistance" : 25 * mm});
        }
        {
            var Q0;
            Q0=makeQuery(id+"F13.opBoolean","MERGE",FACE,{"derivedFrom":[makeQuery(id+"F7.opExtrude","SWEPT_FACE",FACE,{"disambiguationData":[OSD([sQuery(id+"F6.wireOp",EDGE,"E81.right")])]}),makeQuery(id+"F10.opExtrude","SWEPT_FACE",FACE,{"disambiguationData":[OSD([sQuery(id+"F9.wireOp",EDGE,"E82.0")])]}),makeQuery(id+"F10.opExtrude","SWEPT_FACE",FACE,{"disambiguationData":[OSD([sQuery(id+"F9.wireOp",EDGE,"E86.0")])]}),makeQuery(id+"F10.opExtrude","SWEPT_FACE",FACE,{"disambiguationData":[OSD([sQuery(id+"F9.wireOp",EDGE,"E90.0")])]}),makeQuery(id+"F10.opExtrude","SWEPT_FACE",FACE,{"disambiguationData":[OSD([sQuery(id+"F9.wireOp",EDGE,"E94.0")])]}),makeQuery(id+"F10.opExtrude","SWEPT_FACE",FACE,{"disambiguationData":[OSD([sQuery(id+"F9.wireOp",EDGE,"E98.0")])]}),makeQuery(id+"F10.opExtrude","SWEPT_FACE",FACE,{"disambiguationData":[OSD([sQuery(id+"F9.wireOp",EDGE,"E102.0")])]}),makeQuery(id+"F12.opExtrude","SWEPT_FACE",FACE,{"disambiguationData":[OSD([sQuery(id+"F11.wireOp",EDGE,"E106.left")])]})]});
            var sketch = newSketch(context, id + "F30", { "sketchPlane" : qUnion([Q0])});
            skLineSegment(sketch, "E163.bottom", {"start": v(-103, -74.31) * mm, "end": v(-99, -74.31) * mm});
            skLineSegment(sketch, "E163.top", {"start": v(-103, -62.15) * mm, "end": v(-99, -62.15) * mm});
            skLineSegment(sketch, "E163.left", {"start": v(-103, -74.31) * mm, "end": v(-103, -62.15) * mm});
            skLineSegment(sketch, "E163.right", {"start": v(-99, -74.31) * mm, "end": v(-99, -62.15) * mm});
            skLineSegment(sketch, "E164.1.0.0", {"start": v(-98.97, -44.71) * mm, "end": v(-98.97, -32.55) * mm});
            skLineSegment(sketch, "E164.1.0.1", {"start": v(-102.97, -44.71) * mm, "end": v(-98.97, -44.71) * mm});
            skLineSegment(sketch, "E164.1.0.2", {"start": v(-102.97, -44.71) * mm, "end": v(-102.97, -32.55) * mm});
            skLineSegment(sketch, "E164.1.0.3", {"start": v(-102.97, -32.55) * mm, "end": v(-98.97, -32.55) * mm});
            skLineSegment(sketch, "E164.2.0.0", {"start": v(-98.94, -15.11) * mm, "end": v(-98.94, -2.95) * mm});
            skLineSegment(sketch, "E164.2.0.1", {"start": v(-102.94, -15.11) * mm, "end": v(-98.94, -15.11) * mm});
            skLineSegment(sketch, "E164.2.0.2", {"start": v(-102.94, -15.11) * mm, "end": v(-102.94, -2.95) * mm});
            skLineSegment(sketch, "E164.2.0.3", {"start": v(-102.94, -2.95) * mm, "end": v(-98.94, -2.95) * mm});
            skLineSegment(sketch, "E164.3.0.0", {"start": v(-98.9, 14.49) * mm, "end": v(-98.9, 26.65) * mm});
            skLineSegment(sketch, "E164.3.0.1", {"start": v(-102.9, 14.49) * mm, "end": v(-98.9, 14.49) * mm});
            skLineSegment(sketch, "E164.3.0.2", {"start": v(-102.9, 14.49) * mm, "end": v(-102.9, 26.65) * mm});
            skLineSegment(sketch, "E164.3.0.3", {"start": v(-102.9, 26.65) * mm, "end": v(-98.9, 26.65) * mm});
            skLineSegment(sketch, "E164.4.0.0", {"start": v(-98.88, 44.09) * mm, "end": v(-98.88, 56.25) * mm});
            skLineSegment(sketch, "E164.4.0.1", {"start": v(-102.88, 44.09) * mm, "end": v(-98.88, 44.09) * mm});
            skLineSegment(sketch, "E164.4.0.2", {"start": v(-102.88, 44.09) * mm, "end": v(-102.88, 56.25) * mm});
            skLineSegment(sketch, "E164.4.0.3", {"start": v(-102.88, 56.25) * mm, "end": v(-98.88, 56.25) * mm});
            skLineSegment(sketch, "E164.5.0.0", {"start": v(-98.85, 73.69) * mm, "end": v(-98.85, 85.85) * mm});
            skLineSegment(sketch, "E164.5.0.1", {"start": v(-102.85, 73.69) * mm, "end": v(-98.85, 73.69) * mm});
            skLineSegment(sketch, "E164.5.0.2", {"start": v(-102.85, 73.69) * mm, "end": v(-102.85, 85.85) * mm});
            skLineSegment(sketch, "E164.5.0.3", {"start": v(-102.85, 85.85) * mm, "end": v(-98.85, 85.85) * mm});
            skLineSegment(sketch, "E164.direction1", {"start": v(-99, -74.31) * mm, "end": v(-98.97, -44.71) * mm, "construction": true});
            skSolve(sketch);
        }
        {
            var Q0;
            Q0 = qSketchRegion(id + "F30", true);
            var Q1;
            Q1=makeQuery(id+"F12.opExtrude","SWEPT_FACE",FACE,{"disambiguationData":[OSD([sQuery(id+"F11.wireOp",EDGE,"E106.right")])]});
            extrude(context, id + "F31", {"entities" : qUnion([Q0]), "operationType" : NewBodyOperationType.REMOVE, "endBound" : BoundingType.UP_TO_SURFACE, "oppositeDirection" : true, "depth" : 25 * mm, "endBoundEntityFace" : qUnion([Q1]), "offsetDistance" : 25 * mm});
        }
        {
            var Q0;
            Q0=makeQuery(id+"F31.boolean.opBoolean","COPY",FACE,{"derivedFrom":makeQuery(id+"F31.opExtrude","SWEPT_FACE",FACE,{"disambiguationData":[OSD([sQuery(id+"F30.wireOp",EDGE,"E164.1.0.2")])]})});
            var Q1;
            Q1=makeQuery(id+"F31.boolean.opBoolean","COPY",FACE,{"derivedFrom":makeQuery(id+"F31.opExtrude","SWEPT_FACE",FACE,{"disambiguationData":[OSD([sQuery(id+"F30.wireOp",EDGE,"E164.2.0.2")])]})});
            var Q2;
            Q2=makeQuery(id+"F31.boolean.opBoolean","COPY",FACE,{"derivedFrom":makeQuery(id+"F31.opExtrude","SWEPT_FACE",FACE,{"disambiguationData":[OSD([sQuery(id+"F30.wireOp",EDGE,"E164.3.0.2")])]})});
            var Q3;
            Q3=makeQuery(id+"F31.boolean.opBoolean","COPY",FACE,{"derivedFrom":makeQuery(id+"F31.opExtrude","SWEPT_FACE",FACE,{"disambiguationData":[OSD([sQuery(id+"F30.wireOp",EDGE,"E164.4.0.2")])]})});
            var Q4;
            Q4=makeQuery(id+"F31.boolean.opBoolean","COPY",FACE,{"derivedFrom":makeQuery(id+"F31.opExtrude","SWEPT_FACE",FACE,{"disambiguationData":[OSD([sQuery(id+"F30.wireOp",EDGE,"E164.5.0.2")])]})});
            var Q5;
            {var subQ0=sQuery(id+"F11.wireOp",EDGE,"E106.right");var subQ5=sQuery(id+"F6.wireOp",EDGE,"E81.right");var subQ6=makeQuery(id+"F7.opExtrude","SWEPT_FACE",FACE,{"disambiguationData":[OSD([subQ5])]});var subQ8=sQuery(id+"F6.wireOp",EDGE,"E81.top");var subQ17=sQuery(id+"F11.wireOp",EDGE,"E106.left");var subQ21=sQuery(id+"F16.wireOp",EDGE,"E131.top");var subQ23=sQuery(id+"F11.wireOp",EDGE,"E106.top");var subQ25=sQuery(id+"F21.wireOp",EDGE,"E156.right");var subQ37=sQuery(id+"F16.wireOp",EDGE,"E131.bottom");var subQ40=sQuery(id+"F16.wireOp",EDGE,"E131.right");var subQ41=sQuery(id+"F6.wireOp",EDGE,"E81.left");var subQ42=sQuery(id+"F21.wireOp",EDGE,"E156.left");Q5=makeQuery(id+"F31.boolean.opBoolean","SPLIT",FACE,{"disambiguationData":[TD([makeQuery(id+"F31.opExtrude","SWEPT_FACE",FACE,{"disambiguationData":[OSD([sQuery(id+"F30.wireOp",EDGE,"E163.top")])]})])],"derivedFrom":makeQuery(id+"F29.boolean.opBoolean","SPLIT",FACE,{"disambiguationData":[TD([subQ6])],"derivedFrom":makeQuery(id+"F27.boolean.opBoolean","SPLIT",FACE,{"disambiguationData":[TD([subQ6])],"derivedFrom":makeQuery(id+"F25.boolean.opBoolean","SPLIT",FACE,{"disambiguationData":[TD([makeQuery(id+"F7.opExtrude","SWEPT_FACE",FACE,{"disambiguationData":[OSD([subQ41])]})])],"derivedFrom":makeQuery(id+"F23.opBoolean","MERGE",FACE,{"derivedFrom":[makeQuery(id+"F18.opBoolean","MERGE",FACE,{"derivedFrom":[makeQuery(id+"F13.opBoolean","MERGE",FACE,{"derivedFrom":[makeQuery(id+"F7.opExtrude","CAP_FACE",FACE,{"disambiguationData":[OSD([sQuery(id+"F6.wireOp",EDGE,"E81.bottom"),subQ8,subQ41,subQ5])],"isStart":false}),makeQuery(id+"F12.opExtrude","CAP_FACE",FACE,{"disambiguationData":[OSD([sQuery(id+"F11.wireOp",EDGE,"E106.bottom"),subQ23,subQ17,subQ0])],"isStart":false})]}),makeQuery(id+"F17.opExtrude","CAP_FACE",FACE,{"disambiguationData":[OSD([subQ37,subQ21,sQuery(id+"F16.wireOp",EDGE,"E131.left"),subQ40])],"isStart":false})]}),makeQuery(id+"F22.opExtrude","CAP_FACE",FACE,{"disambiguationData":[OSD([sQuery(id+"F21.wireOp",EDGE,"E156.bottom"),sQuery(id+"F21.wireOp",EDGE,"E156.top"),subQ42,subQ25])],"isStart":false})]})})})})});}
            extrude(context, id + "F32", {"entities" : qUnion([Q0, Q1, Q2, Q3, Q4]), "operationType" : NewBodyOperationType.REMOVE, "endBound" : BoundingType.UP_TO_SURFACE, "oppositeDirection" : true, "depth" : 25 * mm, "endBoundEntityFace" : qUnion([Q5]), "offsetDistance" : 25 * mm});
        }
        {
            var Q0;
            Q0=makeQuery(id+"F1.opExtrude","CAP_FACE",FACE,{"disambiguationData":[OSD([sQuery(id+"F0.wireOp",EDGE,"E0.bottom"),sQuery(id+"F0.wireOp",EDGE,"E0.top"),sQuery(id+"F0.wireOp",EDGE,"E0.left"),sQuery(id+"F0.wireOp",EDGE,"E0.right")])],"isStart":false});
            var sketch = newSketch(context, id + "F33", { "sketchPlane" : qUnion([Q0])});
            skLineSegment(sketch, "E165.bottom", {"start": v(-34.5, -70) * mm, "end": v(34.5, -70) * mm});
            skLineSegment(sketch, "E165.top", {"start": v(-34.5, -41) * mm, "end": v(34.5, -41) * mm});
            skLineSegment(sketch, "E165.left", {"start": v(-34.5, -70) * mm, "end": v(-34.5, -41) * mm});
            skLineSegment(sketch, "E165.right", {"start": v(34.5, -70) * mm, "end": v(34.5, -41) * mm});
            skPoint(sketch, "E165.middle", {"position": v(0, -55.5) * mm});
            skLineSegment(sketch, "E166", {"start": v(-100, 0) * mm, "end": v(100, 0) * mm, "construction": true});
            skLineSegment(sketch, "E167.MirrorCS", {"start": v(-34.5, 41) * mm, "end": v(34.5, 41) * mm});
            skLineSegment(sketch, "E168.MirrorCS", {"start": v(-34.5, 70) * mm, "end": v(-34.5, 41) * mm});
            skLineSegment(sketch, "E169.MirrorCS", {"start": v(-34.5, 70) * mm, "end": v(34.5, 70) * mm});
            skLineSegment(sketch, "E170.MirrorCS", {"start": v(34.5, 70) * mm, "end": v(34.5, 41) * mm});
            skSolve(sketch);
        }
        {
            var Q0;
            Q0 = qSketchRegion(id + "F33", true);
            var Q1;
            Q1=makeQuery(id+"F1.opExtrude","CAP_FACE",FACE,{"disambiguationData":[OSD([sQuery(id+"F0.wireOp",EDGE,"E0.bottom"),sQuery(id+"F0.wireOp",EDGE,"E0.top"),sQuery(id+"F0.wireOp",EDGE,"E0.left"),sQuery(id+"F0.wireOp",EDGE,"E0.right")])],"isStart":true});
            extrude(context, id + "F34", {"entities" : qUnion([Q0]), "operationType" : NewBodyOperationType.REMOVE, "endBound" : BoundingType.UP_TO_SURFACE, "oppositeDirection" : true, "depth" : 25 * mm, "endBoundEntityFace" : qUnion([Q1]), "offsetDistance" : 25 * mm});
        }
        {
            var Q0;
            Q0=makeQuery(id+"F1.opExtrude","CAP_FACE",FACE,{"disambiguationData":[OSD([sQuery(id+"F0.wireOp",EDGE,"E0.bottom"),sQuery(id+"F0.wireOp",EDGE,"E0.top"),sQuery(id+"F0.wireOp",EDGE,"E0.left"),sQuery(id+"F0.wireOp",EDGE,"E0.right")])],"isStart":false});
            var sketch = newSketch(context, id + "F35", { "sketchPlane" : qUnion([Q0])});
            skLineSegment(sketch, "E171.bottom", {"start": v(-38.04, -209.2) * mm, "end": v(-238.04, -209.2) * mm});
            skLineSegment(sketch, "E171.top", {"start": v(-38.04, -409.2) * mm, "end": v(-238.04, -409.2) * mm});
            skLineSegment(sketch, "E171.left", {"start": v(-38.04, -209.2) * mm, "end": v(-38.04, -409.2) * mm});
            skLineSegment(sketch, "E171.right", {"start": v(-238.04, -209.2) * mm, "end": v(-238.04, -409.2) * mm});
            skPoint(sketch, "E171.middle", {"position": v(-138.04, -309.2) * mm});
            skSolve(sketch);
        }
        {
            var Q0;
            Q0 = qSketchRegion(id + "F35", true);
            extrude(context, id + "F36", {"entities" : qUnion([Q0]), "depth" : 3 * mm, "offsetDistance" : 25 * mm});
        }
        {
            var Q0;
            Q0=makeQuery(id+"F36.opExtrude","CAP_FACE",FACE,{"disambiguationData":[OSD([sQuery(id+"F35.wireOp",EDGE,"E171.bottom"),sQuery(id+"F35.wireOp",EDGE,"E171.top"),sQuery(id+"F35.wireOp",EDGE,"E171.left"),sQuery(id+"F35.wireOp",EDGE,"E171.right")])],"isStart":false});
            var sketch = newSketch(context, id + "F37", { "sketchPlane" : qUnion([Q0])});
            skLineSegment(sketch, "E172.bottom", {"start": v(-235.31, -405.64) * mm, "end": v(-231.31, -405.64) * mm});
            skLineSegment(sketch, "E172.top", {"start": v(-235.31, -393.48) * mm, "end": v(-231.31, -393.48) * mm});
            skLineSegment(sketch, "E172.left", {"start": v(-235.31, -405.64) * mm, "end": v(-235.31, -393.48) * mm});
            skLineSegment(sketch, "E172.right", {"start": v(-231.31, -405.64) * mm, "end": v(-231.31, -393.48) * mm});
            skLineSegment(sketch, "E173.1.0.0", {"start": v(-235.19, -369.44) * mm, "end": v(-235.19, -357.28) * mm});
            skLineSegment(sketch, "E173.1.0.1", {"start": v(-231.19, -369.44) * mm, "end": v(-231.19, -357.28) * mm});
            skLineSegment(sketch, "E173.1.0.2", {"start": v(-235.19, -369.44) * mm, "end": v(-231.19, -369.44) * mm});
            skLineSegment(sketch, "E173.1.0.3", {"start": v(-235.19, -357.28) * mm, "end": v(-231.19, -357.28) * mm});
            skLineSegment(sketch, "E173.2.0.0", {"start": v(-235.06, -333.24) * mm, "end": v(-235.06, -321.08) * mm});
            skLineSegment(sketch, "E173.2.0.1", {"start": v(-231.06, -333.24) * mm, "end": v(-231.06, -321.08) * mm});
            skLineSegment(sketch, "E173.2.0.2", {"start": v(-235.06, -333.24) * mm, "end": v(-231.06, -333.24) * mm});
            skLineSegment(sketch, "E173.2.0.3", {"start": v(-235.06, -321.08) * mm, "end": v(-231.06, -321.08) * mm});
            skLineSegment(sketch, "E173.3.0.0", {"start": v(-234.93, -297.04) * mm, "end": v(-234.93, -284.88) * mm});
            skLineSegment(sketch, "E173.3.0.1", {"start": v(-230.93, -297.04) * mm, "end": v(-230.93, -284.88) * mm});
            skLineSegment(sketch, "E173.3.0.2", {"start": v(-234.93, -297.04) * mm, "end": v(-230.93, -297.04) * mm});
            skLineSegment(sketch, "E173.3.0.3", {"start": v(-234.93, -284.88) * mm, "end": v(-230.93, -284.88) * mm});
            skLineSegment(sketch, "E173.4.0.0", {"start": v(-234.8, -260.84) * mm, "end": v(-234.8, -248.68) * mm});
            skLineSegment(sketch, "E173.4.0.1", {"start": v(-230.8, -260.84) * mm, "end": v(-230.8, -248.68) * mm});
            skLineSegment(sketch, "E173.4.0.2", {"start": v(-234.8, -260.84) * mm, "end": v(-230.8, -260.84) * mm});
            skLineSegment(sketch, "E173.4.0.3", {"start": v(-234.8, -248.68) * mm, "end": v(-230.8, -248.68) * mm});
            skLineSegment(sketch, "E173.5.0.0", {"start": v(-234.68, -224.64) * mm, "end": v(-234.68, -212.48) * mm});
            skLineSegment(sketch, "E173.5.0.1", {"start": v(-230.68, -224.64) * mm, "end": v(-230.68, -212.48) * mm});
            skLineSegment(sketch, "E173.5.0.2", {"start": v(-234.68, -224.64) * mm, "end": v(-230.68, -224.64) * mm});
            skLineSegment(sketch, "E173.5.0.3", {"start": v(-234.68, -212.48) * mm, "end": v(-230.68, -212.48) * mm});
            skLineSegment(sketch, "E173.direction1", {"start": v(-235.31, -405.64) * mm, "end": v(-235.19, -369.44) * mm, "construction": true});
            skLineSegment(sketch, "E174", {"start": v(-138.04, -409.2) * mm, "end": v(-138.04, -209.2) * mm, "construction": true});
            skLineSegment(sketch, "E175", {"start": v(-38.04, -309.2) * mm, "end": v(-238.04, -309.2) * mm, "construction": true});
            skLineSegment(sketch, "E176.MirrorCS", {"start": v(-40.77, -405.64) * mm, "end": v(-40.77, -393.48) * mm});
            skLineSegment(sketch, "E177.MirrorCS", {"start": v(-40.77, -393.48) * mm, "end": v(-44.77, -393.48) * mm});
            skLineSegment(sketch, "E178.MirrorCS", {"start": v(-44.77, -405.64) * mm, "end": v(-44.77, -393.48) * mm});
            skLineSegment(sketch, "E179.MirrorCS", {"start": v(-40.77, -405.64) * mm, "end": v(-44.77, -405.64) * mm});
            skLineSegment(sketch, "E180.MirrorCS", {"start": v(-40.9, -369.44) * mm, "end": v(-40.9, -357.28) * mm});
            skLineSegment(sketch, "E181.MirrorCS", {"start": v(-40.9, -369.44) * mm, "end": v(-44.9, -369.44) * mm});
            skLineSegment(sketch, "E182.MirrorCS", {"start": v(-44.9, -369.44) * mm, "end": v(-44.9, -357.28) * mm});
            skLineSegment(sketch, "E183.MirrorCS", {"start": v(-40.9, -357.28) * mm, "end": v(-44.9, -357.28) * mm});
            skLineSegment(sketch, "E184.MirrorCS", {"start": v(-41.02, -333.24) * mm, "end": v(-41.02, -321.08) * mm});
            skLineSegment(sketch, "E185.MirrorCS", {"start": v(-41.02, -333.24) * mm, "end": v(-45.02, -333.24) * mm});
            skLineSegment(sketch, "E186.MirrorCS", {"start": v(-45.02, -333.24) * mm, "end": v(-45.02, -321.08) * mm});
            skLineSegment(sketch, "E187.MirrorCS", {"start": v(-41.02, -321.08) * mm, "end": v(-45.02, -321.08) * mm});
            skLineSegment(sketch, "E188.MirrorCS", {"start": v(-41.15, -297.04) * mm, "end": v(-41.15, -284.88) * mm});
            skLineSegment(sketch, "E189.MirrorCS", {"start": v(-41.15, -297.04) * mm, "end": v(-45.15, -297.04) * mm});
            skLineSegment(sketch, "E190.MirrorCS", {"start": v(-45.15, -297.04) * mm, "end": v(-45.15, -284.88) * mm});
            skLineSegment(sketch, "E191.MirrorCS", {"start": v(-41.15, -284.88) * mm, "end": v(-45.15, -284.88) * mm});
            skLineSegment(sketch, "E192.MirrorCS", {"start": v(-41.27, -260.84) * mm, "end": v(-41.27, -248.68) * mm});
            skLineSegment(sketch, "E193.MirrorCS", {"start": v(-41.27, -260.84) * mm, "end": v(-45.27, -260.84) * mm});
            skLineSegment(sketch, "E194.MirrorCS", {"start": v(-45.27, -260.84) * mm, "end": v(-45.27, -248.68) * mm});
            skLineSegment(sketch, "E195.MirrorCS", {"start": v(-41.27, -248.68) * mm, "end": v(-45.27, -248.68) * mm});
            skLineSegment(sketch, "E196.MirrorCS", {"start": v(-41.4, -224.64) * mm, "end": v(-41.4, -212.48) * mm});
            skLineSegment(sketch, "E197.MirrorCS", {"start": v(-41.4, -224.64) * mm, "end": v(-45.4, -224.64) * mm});
            skLineSegment(sketch, "E198.MirrorCS", {"start": v(-45.4, -224.64) * mm, "end": v(-45.4, -212.48) * mm});
            skLineSegment(sketch, "E199.MirrorCS", {"start": v(-41.4, -212.48) * mm, "end": v(-45.4, -212.48) * mm});
            skLineSegment(sketch, "E200.bottom", {"start": v(-224.2, -212.48) * mm, "end": v(-212.03, -212.48) * mm});
            skLineSegment(sketch, "E200.top", {"start": v(-224.2, -216.48) * mm, "end": v(-212.03, -216.48) * mm});
            skLineSegment(sketch, "E200.left", {"start": v(-224.2, -212.48) * mm, "end": v(-224.2, -216.48) * mm});
            skLineSegment(sketch, "E200.right", {"start": v(-212.03, -212.48) * mm, "end": v(-212.03, -216.48) * mm});
            skLineSegment(sketch, "E201.1.0.0", {"start": v(-192, -212.48) * mm, "end": v(-179.83, -212.48) * mm});
            skLineSegment(sketch, "E201.1.0.1", {"start": v(-179.83, -212.48) * mm, "end": v(-179.83, -216.48) * mm});
            skLineSegment(sketch, "E201.1.0.2", {"start": v(-192, -216.48) * mm, "end": v(-179.83, -216.48) * mm});
            skLineSegment(sketch, "E201.1.0.3", {"start": v(-192, -212.48) * mm, "end": v(-192, -216.48) * mm});
            skLineSegment(sketch, "E201.2.0.0", {"start": v(-159.8, -212.48) * mm, "end": v(-147.63, -212.48) * mm});
            skLineSegment(sketch, "E201.2.0.1", {"start": v(-147.63, -212.48) * mm, "end": v(-147.63, -216.48) * mm});
            skLineSegment(sketch, "E201.2.0.2", {"start": v(-159.8, -216.48) * mm, "end": v(-147.63, -216.48) * mm});
            skLineSegment(sketch, "E201.2.0.3", {"start": v(-159.8, -212.48) * mm, "end": v(-159.8, -216.48) * mm});
            skLineSegment(sketch, "E201.3.0.0", {"start": v(-127.6, -212.48) * mm, "end": v(-115.43, -212.48) * mm});
            skLineSegment(sketch, "E201.3.0.1", {"start": v(-115.43, -212.48) * mm, "end": v(-115.43, -216.48) * mm});
            skLineSegment(sketch, "E201.3.0.2", {"start": v(-127.6, -216.48) * mm, "end": v(-115.43, -216.48) * mm});
            skLineSegment(sketch, "E201.3.0.3", {"start": v(-127.6, -212.48) * mm, "end": v(-127.6, -216.48) * mm});
            skLineSegment(sketch, "E201.4.0.0", {"start": v(-95.4, -212.48) * mm, "end": v(-83.23, -212.48) * mm});
            skLineSegment(sketch, "E201.4.0.1", {"start": v(-83.23, -212.48) * mm, "end": v(-83.23, -216.48) * mm});
            skLineSegment(sketch, "E201.4.0.2", {"start": v(-95.4, -216.48) * mm, "end": v(-83.23, -216.48) * mm});
            skLineSegment(sketch, "E201.4.0.3", {"start": v(-95.4, -212.48) * mm, "end": v(-95.4, -216.48) * mm});
            skLineSegment(sketch, "E201.5.0.0", {"start": v(-63.2, -212.48) * mm, "end": v(-51.03, -212.48) * mm});
            skLineSegment(sketch, "E201.5.0.1", {"start": v(-51.03, -212.48) * mm, "end": v(-51.03, -216.48) * mm});
            skLineSegment(sketch, "E201.5.0.2", {"start": v(-63.2, -216.48) * mm, "end": v(-51.03, -216.48) * mm});
            skLineSegment(sketch, "E201.5.0.3", {"start": v(-63.2, -212.48) * mm, "end": v(-63.2, -216.48) * mm});
            skLineSegment(sketch, "E201.direction1", {"start": v(-224.2, -212.48) * mm, "end": v(-192, -212.48) * mm, "construction": true});
            skLineSegment(sketch, "E202.MirrorCS", {"start": v(-224.2, -405.93) * mm, "end": v(-224.2, -401.93) * mm});
            skLineSegment(sketch, "E203.MirrorCS", {"start": v(-224.2, -401.93) * mm, "end": v(-212.03, -401.93) * mm});
            skLineSegment(sketch, "E204.MirrorCS", {"start": v(-212.03, -405.93) * mm, "end": v(-212.03, -401.93) * mm});
            skLineSegment(sketch, "E205.MirrorCS", {"start": v(-224.2, -405.93) * mm, "end": v(-212.03, -405.93) * mm});
            skLineSegment(sketch, "E206.MirrorCS", {"start": v(-192, -405.93) * mm, "end": v(-192, -401.93) * mm});
            skLineSegment(sketch, "E207.MirrorCS", {"start": v(-192, -401.93) * mm, "end": v(-179.83, -401.93) * mm});
            skLineSegment(sketch, "E208.MirrorCS", {"start": v(-192, -405.93) * mm, "end": v(-179.83, -405.93) * mm});
            skLineSegment(sketch, "E209.MirrorCS", {"start": v(-179.83, -405.93) * mm, "end": v(-179.83, -401.93) * mm});
            skLineSegment(sketch, "E210.MirrorCS", {"start": v(-159.8, -405.93) * mm, "end": v(-147.63, -405.93) * mm});
            skLineSegment(sketch, "E211.MirrorCS", {"start": v(-159.8, -405.93) * mm, "end": v(-159.8, -401.93) * mm});
            skLineSegment(sketch, "E212.MirrorCS", {"start": v(-159.8, -401.93) * mm, "end": v(-147.63, -401.93) * mm});
            skLineSegment(sketch, "E213.MirrorCS", {"start": v(-147.63, -405.93) * mm, "end": v(-147.63, -401.93) * mm});
            skLineSegment(sketch, "E214.MirrorCS", {"start": v(-127.6, -405.93) * mm, "end": v(-115.43, -405.93) * mm});
            skLineSegment(sketch, "E215.MirrorCS", {"start": v(-127.6, -405.93) * mm, "end": v(-127.6, -401.93) * mm});
            skLineSegment(sketch, "E216.MirrorCS", {"start": v(-127.6, -401.93) * mm, "end": v(-115.43, -401.93) * mm});
            skLineSegment(sketch, "E217.MirrorCS", {"start": v(-115.43, -405.93) * mm, "end": v(-115.43, -401.93) * mm});
            skLineSegment(sketch, "E218.MirrorCS", {"start": v(-95.4, -405.93) * mm, "end": v(-83.23, -405.93) * mm});
            skLineSegment(sketch, "E219.MirrorCS", {"start": v(-95.4, -405.93) * mm, "end": v(-95.4, -401.93) * mm});
            skLineSegment(sketch, "E220.MirrorCS", {"start": v(-95.4, -401.93) * mm, "end": v(-83.23, -401.93) * mm});
            skLineSegment(sketch, "E221.MirrorCS", {"start": v(-83.23, -405.93) * mm, "end": v(-83.23, -401.93) * mm});
            skLineSegment(sketch, "E222.MirrorCS", {"start": v(-63.2, -405.93) * mm, "end": v(-51.03, -405.93) * mm});
            skLineSegment(sketch, "E223.MirrorCS", {"start": v(-63.2, -405.93) * mm, "end": v(-63.2, -401.93) * mm});
            skLineSegment(sketch, "E224.MirrorCS", {"start": v(-63.2, -401.93) * mm, "end": v(-51.03, -401.93) * mm});
            skLineSegment(sketch, "E225.MirrorCS", {"start": v(-51.03, -405.93) * mm, "end": v(-51.03, -401.93) * mm});
            skSolve(sketch);
        }
        {
            var Q0;
            Q0 = qSketchRegion(id + "F37", true);
            var Q1;
            Q1=makeQuery(id+"F36.opExtrude","CAP_FACE",FACE,{"disambiguationData":[OSD([sQuery(id+"F35.wireOp",EDGE,"E171.bottom"),sQuery(id+"F35.wireOp",EDGE,"E171.top"),sQuery(id+"F35.wireOp",EDGE,"E171.left"),sQuery(id+"F35.wireOp",EDGE,"E171.right")])],"isStart":true});
            extrude(context, id + "F38", {"entities" : qUnion([Q0]), "operationType" : NewBodyOperationType.REMOVE, "endBound" : BoundingType.UP_TO_SURFACE, "oppositeDirection" : true, "depth" : 25 * mm, "endBoundEntityFace" : qUnion([Q1]), "offsetDistance" : 25 * mm});
        }
    });
